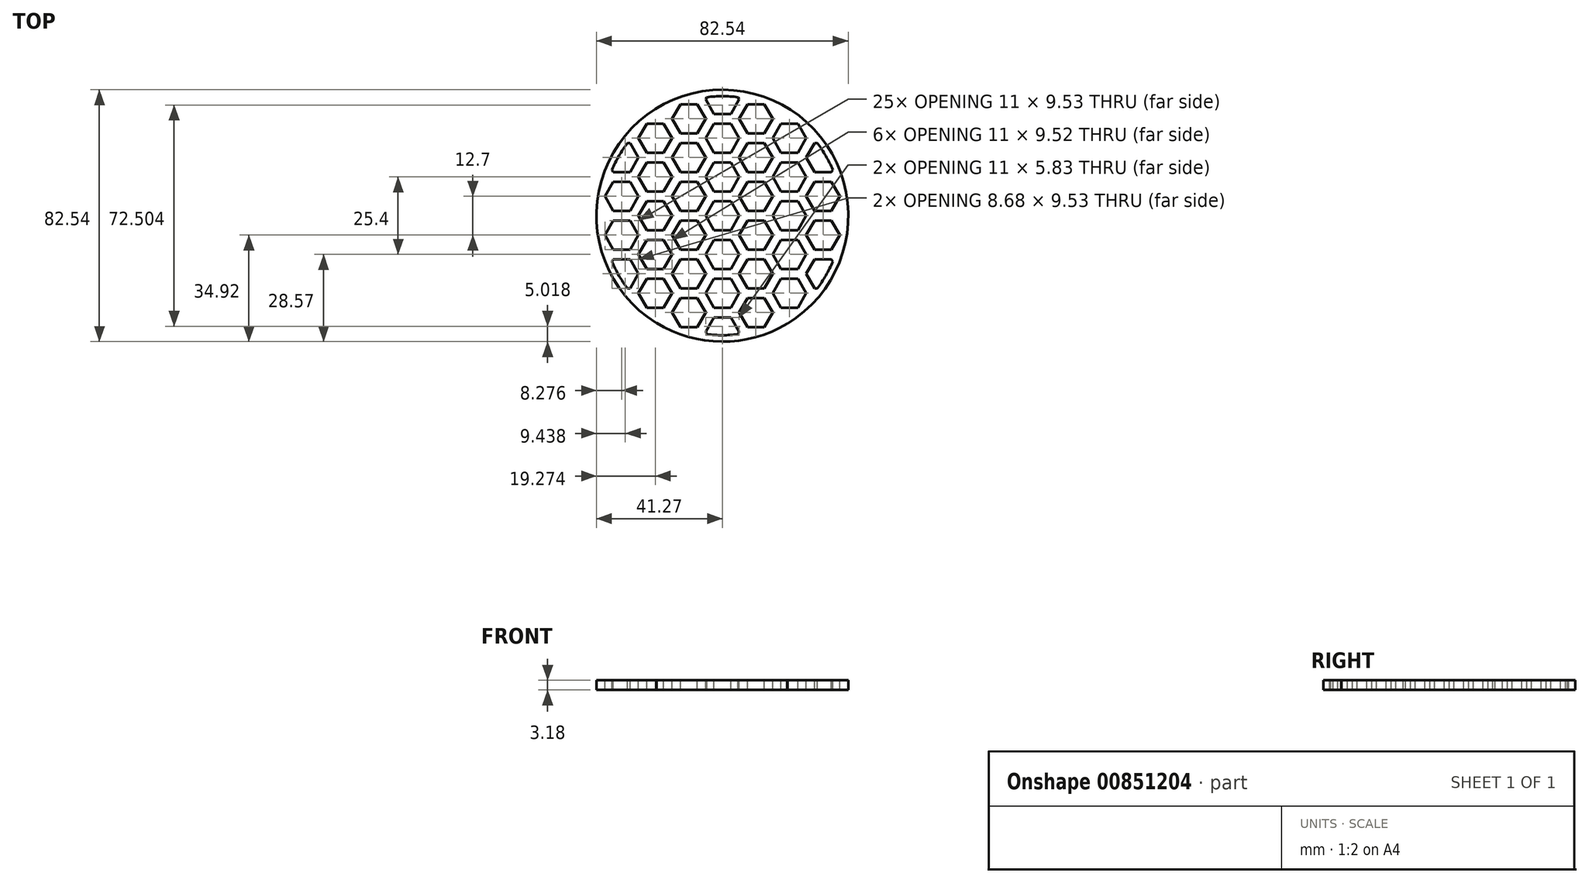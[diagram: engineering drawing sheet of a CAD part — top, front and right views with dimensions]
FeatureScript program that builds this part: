
annotation { "Feature Type Name" : "Feature", "Feature Type Description" : "" }
export const myFeature = defineFeature(function(context is Context, id is Id, definition is map)
    precondition{}
    {
        {
            var Q0;
            Q0=qCreatedBy(makeId("Top.planeOp"),FACE);
            var sketch = newSketch(context, id + "F0", { "sketchPlane" : qUnion([Q0])});
            skCircle(sketch, "E0", {"center": v(0, 0) * mm, "radius": 41.27 * mm});
            skSolve(sketch);
        }
        {
            var Q0;
            Q0 = qSketchRegion(id + "F0", true);
            extrude(context, id + "F1", {"entities" : qUnion([Q0]), "depth" : 3.17 * mm, "offsetDistance" : 25.4 * mm});
        }
        {
            var Q0;
            Q0=makeQuery(id+"F1.opExtrude","CAP_FACE",FACE,{"disambiguationData":[OSD([sQuery(id+"F0.wireOp",EDGE,"E0")])],"isStart":false});
            var sketch = newSketch(context, id + "F2", { "sketchPlane" : qUnion([Q0])});
            skCircle(sketch, "E1.cCircle", {"center": v(-44, -50.8) * mm, "radius": 4.76 * mm, "construction": true});
            skLineSegment(sketch, "E1.0", {"start": v(-46.74, -46.04) * mm, "end": v(-41.24, -46.04) * mm});
            skLineSegment(sketch, "E1.1", {"start": v(-41.24, -46.04) * mm, "end": v(-38.5, -50.8) * mm});
            skLineSegment(sketch, "E1.2", {"start": v(-38.5, -50.8) * mm, "end": v(-41.24, -55.56) * mm});
            skLineSegment(sketch, "E1.3", {"start": v(-41.24, -55.56) * mm, "end": v(-46.74, -55.56) * mm});
            skLineSegment(sketch, "E1.4", {"start": v(-46.74, -55.56) * mm, "end": v(-49.5, -50.8) * mm});
            skLineSegment(sketch, "E1.5", {"start": v(-49.5, -50.8) * mm, "end": v(-46.74, -46.04) * mm});
            skPoint(sketch, "E1.0.midPoint", {"position": v(-44, -46.04) * mm});
            skCircle(sketch, "E2.cCircle", {"center": v(-33, -44.45) * mm, "radius": 4.76 * mm, "construction": true});
            skLineSegment(sketch, "E2.0", {"start": v(-35.74, -39.69) * mm, "end": v(-30.24, -39.69) * mm});
            skLineSegment(sketch, "E2.1", {"start": v(-30.24, -39.69) * mm, "end": v(-27.5, -44.45) * mm});
            skLineSegment(sketch, "E2.2", {"start": v(-27.5, -44.45) * mm, "end": v(-30.24, -49.21) * mm});
            skLineSegment(sketch, "E2.3", {"start": v(-30.24, -49.21) * mm, "end": v(-35.74, -49.21) * mm});
            skLineSegment(sketch, "E2.4", {"start": v(-35.74, -49.21) * mm, "end": v(-38.5, -44.45) * mm});
            skLineSegment(sketch, "E2.5", {"start": v(-38.5, -44.45) * mm, "end": v(-35.74, -39.69) * mm});
            skPoint(sketch, "E2.0.midPoint", {"position": v(-33, -39.69) * mm});
            skLineSegment(sketch, "E3.0.1.0", {"start": v(-46.74, -33.34) * mm, "end": v(-41.24, -33.34) * mm});
            skLineSegment(sketch, "E3.0.1.1", {"start": v(-41.24, -33.34) * mm, "end": v(-38.5, -38.1) * mm});
            skLineSegment(sketch, "E3.0.1.2", {"start": v(-38.5, -38.1) * mm, "end": v(-41.24, -42.86) * mm});
            skCircle(sketch, "E3.0.1.3", {"center": v(-44, -38.1) * mm, "radius": 4.76 * mm, "construction": true});
            skLineSegment(sketch, "E3.0.1.4", {"start": v(-41.24, -42.86) * mm, "end": v(-46.74, -42.86) * mm});
            skLineSegment(sketch, "E3.0.1.5", {"start": v(-46.74, -42.86) * mm, "end": v(-49.5, -38.1) * mm});
            skLineSegment(sketch, "E3.0.1.6", {"start": v(-49.5, -38.1) * mm, "end": v(-46.74, -33.34) * mm});
            skLineSegment(sketch, "E3.0.2.0", {"start": v(-46.74, -20.64) * mm, "end": v(-41.24, -20.64) * mm});
            skLineSegment(sketch, "E3.0.2.1", {"start": v(-41.24, -20.64) * mm, "end": v(-38.5, -25.4) * mm});
            skLineSegment(sketch, "E3.0.2.2", {"start": v(-38.5, -25.4) * mm, "end": v(-41.24, -30.16) * mm});
            skCircle(sketch, "E3.0.2.3", {"center": v(-44, -25.4) * mm, "radius": 4.76 * mm, "construction": true});
            skLineSegment(sketch, "E3.0.2.4", {"start": v(-41.24, -30.16) * mm, "end": v(-46.74, -30.16) * mm});
            skLineSegment(sketch, "E3.0.2.5", {"start": v(-46.74, -30.16) * mm, "end": v(-49.5, -25.4) * mm});
            skLineSegment(sketch, "E3.0.2.6", {"start": v(-49.5, -25.4) * mm, "end": v(-46.74, -20.64) * mm});
            skLineSegment(sketch, "E3.1.0.0", {"start": v(-24.75, -46.04) * mm, "end": v(-19.25, -46.04) * mm});
            skLineSegment(sketch, "E3.1.0.1", {"start": v(-19.25, -46.04) * mm, "end": v(-16.5, -50.8) * mm});
            skLineSegment(sketch, "E3.1.0.2", {"start": v(-16.5, -50.8) * mm, "end": v(-19.25, -55.56) * mm});
            skCircle(sketch, "E3.1.0.3", {"center": v(-22, -50.8) * mm, "radius": 4.76 * mm, "construction": true});
            skLineSegment(sketch, "E3.1.0.4", {"start": v(-19.25, -55.56) * mm, "end": v(-24.75, -55.56) * mm});
            skLineSegment(sketch, "E3.1.0.5", {"start": v(-24.75, -55.56) * mm, "end": v(-27.5, -50.8) * mm});
            skLineSegment(sketch, "E3.1.0.6", {"start": v(-27.5, -50.8) * mm, "end": v(-24.75, -46.04) * mm});
            skLineSegment(sketch, "E3.1.1.0", {"start": v(-24.75, -33.34) * mm, "end": v(-19.25, -33.34) * mm});
            skLineSegment(sketch, "E3.1.1.1", {"start": v(-19.25, -33.34) * mm, "end": v(-16.5, -38.1) * mm});
            skLineSegment(sketch, "E3.1.1.2", {"start": v(-16.5, -38.1) * mm, "end": v(-19.25, -42.86) * mm});
            skCircle(sketch, "E3.1.1.3", {"center": v(-22, -38.1) * mm, "radius": 4.76 * mm, "construction": true});
            skLineSegment(sketch, "E3.1.1.4", {"start": v(-19.25, -42.86) * mm, "end": v(-24.75, -42.86) * mm});
            skLineSegment(sketch, "E3.1.1.5", {"start": v(-24.75, -42.86) * mm, "end": v(-27.5, -38.1) * mm});
            skLineSegment(sketch, "E3.1.1.6", {"start": v(-27.5, -38.1) * mm, "end": v(-24.75, -33.34) * mm});
            skLineSegment(sketch, "E3.1.2.0", {"start": v(-24.75, -20.64) * mm, "end": v(-19.25, -20.64) * mm});
            skLineSegment(sketch, "E3.1.2.1", {"start": v(-19.25, -20.64) * mm, "end": v(-16.5, -25.4) * mm});
            skLineSegment(sketch, "E3.1.2.2", {"start": v(-16.5, -25.4) * mm, "end": v(-19.25, -30.16) * mm});
            skCircle(sketch, "E3.1.2.3", {"center": v(-22, -25.4) * mm, "radius": 4.76 * mm, "construction": true});
            skLineSegment(sketch, "E3.1.2.4", {"start": v(-19.25, -30.16) * mm, "end": v(-24.75, -30.16) * mm});
            skLineSegment(sketch, "E3.1.2.5", {"start": v(-24.75, -30.16) * mm, "end": v(-27.5, -25.4) * mm});
            skLineSegment(sketch, "E3.1.2.6", {"start": v(-27.5, -25.4) * mm, "end": v(-24.75, -20.64) * mm});
            skLineSegment(sketch, "E3.2.0.0", {"start": v(-2.75, -46.04) * mm, "end": v(2.75, -46.04) * mm});
            skLineSegment(sketch, "E3.2.0.1", {"start": v(2.75, -46.04) * mm, "end": v(5.5, -50.8) * mm});
            skLineSegment(sketch, "E3.2.0.2", {"start": v(5.5, -50.8) * mm, "end": v(2.75, -55.56) * mm});
            skCircle(sketch, "E3.2.0.3", {"center": v(0, -50.8) * mm, "radius": 4.76 * mm, "construction": true});
            skLineSegment(sketch, "E3.2.0.4", {"start": v(2.75, -55.56) * mm, "end": v(-2.75, -55.56) * mm});
            skLineSegment(sketch, "E3.2.0.5", {"start": v(-2.75, -55.56) * mm, "end": v(-5.5, -50.8) * mm});
            skLineSegment(sketch, "E3.2.0.6", {"start": v(-5.5, -50.8) * mm, "end": v(-2.75, -46.04) * mm});
            skLineSegment(sketch, "E3.2.1.0", {"start": v(-2.75, -33.34) * mm, "end": v(2.75, -33.34) * mm});
            skLineSegment(sketch, "E3.2.1.1", {"start": v(2.75, -33.34) * mm, "end": v(5.5, -38.1) * mm});
            skLineSegment(sketch, "E3.2.1.2", {"start": v(5.5, -38.1) * mm, "end": v(2.75, -42.86) * mm});
            skCircle(sketch, "E3.2.1.3", {"center": v(0, -38.1) * mm, "radius": 4.76 * mm, "construction": true});
            skLineSegment(sketch, "E3.2.1.4", {"start": v(2.75, -42.86) * mm, "end": v(-2.75, -42.86) * mm});
            skLineSegment(sketch, "E3.2.1.5", {"start": v(-2.75, -42.86) * mm, "end": v(-5.5, -38.1) * mm});
            skLineSegment(sketch, "E3.2.1.6", {"start": v(-5.5, -38.1) * mm, "end": v(-2.75, -33.34) * mm});
            skLineSegment(sketch, "E3.2.2.0", {"start": v(-2.75, -20.64) * mm, "end": v(2.75, -20.64) * mm});
            skLineSegment(sketch, "E3.2.2.1", {"start": v(2.75, -20.64) * mm, "end": v(5.5, -25.4) * mm});
            skLineSegment(sketch, "E3.2.2.2", {"start": v(5.5, -25.4) * mm, "end": v(2.75, -30.16) * mm});
            skCircle(sketch, "E3.2.2.3", {"center": v(0, -25.4) * mm, "radius": 4.76 * mm, "construction": true});
            skLineSegment(sketch, "E3.2.2.4", {"start": v(2.75, -30.16) * mm, "end": v(-2.75, -30.16) * mm});
            skLineSegment(sketch, "E3.2.2.5", {"start": v(-2.75, -30.16) * mm, "end": v(-5.5, -25.4) * mm});
            skLineSegment(sketch, "E3.2.2.6", {"start": v(-5.5, -25.4) * mm, "end": v(-2.75, -20.64) * mm});
            skLineSegment(sketch, "E3.direction1", {"start": v(-46.74, -55.56) * mm, "end": v(-24.75, -55.56) * mm, "construction": true});
            skLineSegment(sketch, "E3.direction2", {"start": v(-46.74, -55.56) * mm, "end": v(-46.74, -42.86) * mm, "construction": true});
            skLineSegment(sketch, "E4.0.0.3", {"start": v(-46.74, -7.94) * mm, "end": v(-41.24, -7.94) * mm});
            skLineSegment(sketch, "E4.3.0.3", {"start": v(-41.24, -7.94) * mm, "end": v(-38.5, -12.7) * mm});
            skLineSegment(sketch, "E4.6.0.3", {"start": v(-38.5, -12.7) * mm, "end": v(-41.24, -17.46) * mm});
            skCircle(sketch, "E4.9.0.3", {"center": v(-44, -12.7) * mm, "radius": 4.76 * mm, "construction": true});
            skLineSegment(sketch, "E4.11.0.3", {"start": v(-41.24, -17.46) * mm, "end": v(-46.74, -17.46) * mm});
            skLineSegment(sketch, "E4.14.0.3", {"start": v(-46.74, -17.46) * mm, "end": v(-49.5, -12.7) * mm});
            skLineSegment(sketch, "E4.17.0.3", {"start": v(-49.5, -12.7) * mm, "end": v(-46.74, -7.94) * mm});
            skLineSegment(sketch, "E4.0.1.3", {"start": v(-24.75, -7.94) * mm, "end": v(-19.25, -7.94) * mm});
            skLineSegment(sketch, "E4.3.1.3", {"start": v(-19.25, -7.94) * mm, "end": v(-16.5, -12.7) * mm});
            skLineSegment(sketch, "E4.6.1.3", {"start": v(-16.5, -12.7) * mm, "end": v(-19.25, -17.46) * mm});
            skCircle(sketch, "E4.9.1.3", {"center": v(-22, -12.7) * mm, "radius": 4.76 * mm, "construction": true});
            skLineSegment(sketch, "E4.11.1.3", {"start": v(-19.25, -17.46) * mm, "end": v(-24.75, -17.46) * mm});
            skLineSegment(sketch, "E4.14.1.3", {"start": v(-24.75, -17.46) * mm, "end": v(-27.5, -12.7) * mm});
            skLineSegment(sketch, "E4.17.1.3", {"start": v(-27.5, -12.7) * mm, "end": v(-24.75, -7.94) * mm});
            skLineSegment(sketch, "E4.0.2.3", {"start": v(-2.75, -7.94) * mm, "end": v(2.75, -7.94) * mm});
            skLineSegment(sketch, "E4.3.2.3", {"start": v(2.75, -7.94) * mm, "end": v(5.5, -12.7) * mm});
            skLineSegment(sketch, "E4.6.2.3", {"start": v(5.5, -12.7) * mm, "end": v(2.75, -17.46) * mm});
            skCircle(sketch, "E4.9.2.3", {"center": v(0, -12.7) * mm, "radius": 4.76 * mm, "construction": true});
            skLineSegment(sketch, "E4.11.2.3", {"start": v(2.75, -17.46) * mm, "end": v(-2.75, -17.46) * mm});
            skLineSegment(sketch, "E4.14.2.3", {"start": v(-2.75, -17.46) * mm, "end": v(-5.5, -12.7) * mm});
            skLineSegment(sketch, "E4.17.2.3", {"start": v(-5.5, -12.7) * mm, "end": v(-2.75, -7.94) * mm});
            skCircle(sketch, "E5.0.1.0", {"center": v(-33, -31.75) * mm, "radius": 4.76 * mm, "construction": true});
            skLineSegment(sketch, "E5.0.1.1", {"start": v(-38.5, -31.75) * mm, "end": v(-35.74, -26.99) * mm});
            skLineSegment(sketch, "E5.0.1.2", {"start": v(-35.74, -26.99) * mm, "end": v(-30.24, -26.99) * mm});
            skLineSegment(sketch, "E5.0.1.3", {"start": v(-30.24, -26.99) * mm, "end": v(-27.5, -31.75) * mm});
            skLineSegment(sketch, "E5.0.1.4", {"start": v(-27.5, -31.75) * mm, "end": v(-30.24, -36.51) * mm});
            skLineSegment(sketch, "E5.0.1.5", {"start": v(-30.24, -36.51) * mm, "end": v(-35.74, -36.51) * mm});
            skLineSegment(sketch, "E5.0.1.6", {"start": v(-35.74, -36.51) * mm, "end": v(-38.5, -31.75) * mm});
            skCircle(sketch, "E5.0.2.0", {"center": v(-33, -19.05) * mm, "radius": 4.76 * mm, "construction": true});
            skLineSegment(sketch, "E5.0.2.1", {"start": v(-38.5, -19.05) * mm, "end": v(-35.74, -14.29) * mm});
            skLineSegment(sketch, "E5.0.2.2", {"start": v(-35.74, -14.29) * mm, "end": v(-30.24, -14.29) * mm});
            skLineSegment(sketch, "E5.0.2.3", {"start": v(-30.24, -14.29) * mm, "end": v(-27.5, -19.05) * mm});
            skLineSegment(sketch, "E5.0.2.4", {"start": v(-27.5, -19.05) * mm, "end": v(-30.24, -23.81) * mm});
            skLineSegment(sketch, "E5.0.2.5", {"start": v(-30.24, -23.81) * mm, "end": v(-35.74, -23.81) * mm});
            skLineSegment(sketch, "E5.0.2.6", {"start": v(-35.74, -23.81) * mm, "end": v(-38.5, -19.05) * mm});
            skCircle(sketch, "E5.0.3.0", {"center": v(-33, -6.35) * mm, "radius": 4.76 * mm, "construction": true});
            skLineSegment(sketch, "E5.0.3.1", {"start": v(-38.5, -6.35) * mm, "end": v(-35.74, -1.59) * mm});
            skLineSegment(sketch, "E5.0.3.2", {"start": v(-35.74, -1.59) * mm, "end": v(-30.24, -1.59) * mm});
            skLineSegment(sketch, "E5.0.3.3", {"start": v(-30.24, -1.59) * mm, "end": v(-27.5, -6.35) * mm});
            skLineSegment(sketch, "E5.0.3.4", {"start": v(-27.5, -6.35) * mm, "end": v(-30.24, -11.11) * mm});
            skLineSegment(sketch, "E5.0.3.5", {"start": v(-30.24, -11.11) * mm, "end": v(-35.74, -11.11) * mm});
            skLineSegment(sketch, "E5.0.3.6", {"start": v(-35.74, -11.11) * mm, "end": v(-38.5, -6.35) * mm});
            skCircle(sketch, "E5.1.0.0", {"center": v(-11, -44.45) * mm, "radius": 4.76 * mm, "construction": true});
            skLineSegment(sketch, "E5.1.0.1", {"start": v(-16.5, -44.45) * mm, "end": v(-13.75, -39.69) * mm});
            skLineSegment(sketch, "E5.1.0.2", {"start": v(-13.75, -39.69) * mm, "end": v(-8.25, -39.69) * mm});
            skLineSegment(sketch, "E5.1.0.3", {"start": v(-8.25, -39.69) * mm, "end": v(-5.5, -44.45) * mm});
            skLineSegment(sketch, "E5.1.0.4", {"start": v(-5.5, -44.45) * mm, "end": v(-8.25, -49.21) * mm});
            skLineSegment(sketch, "E5.1.0.5", {"start": v(-8.25, -49.21) * mm, "end": v(-13.75, -49.21) * mm});
            skLineSegment(sketch, "E5.1.0.6", {"start": v(-13.75, -49.21) * mm, "end": v(-16.5, -44.45) * mm});
            skCircle(sketch, "E5.1.1.0", {"center": v(-11, -31.75) * mm, "radius": 4.76 * mm, "construction": true});
            skLineSegment(sketch, "E5.1.1.1", {"start": v(-16.5, -31.75) * mm, "end": v(-13.75, -26.99) * mm});
            skLineSegment(sketch, "E5.1.1.2", {"start": v(-13.75, -26.99) * mm, "end": v(-8.25, -26.99) * mm});
            skLineSegment(sketch, "E5.1.1.3", {"start": v(-8.25, -26.99) * mm, "end": v(-5.5, -31.75) * mm});
            skLineSegment(sketch, "E5.1.1.4", {"start": v(-5.5, -31.75) * mm, "end": v(-8.25, -36.51) * mm});
            skLineSegment(sketch, "E5.1.1.5", {"start": v(-8.25, -36.51) * mm, "end": v(-13.75, -36.51) * mm});
            skLineSegment(sketch, "E5.1.1.6", {"start": v(-13.75, -36.51) * mm, "end": v(-16.5, -31.75) * mm});
            skCircle(sketch, "E5.1.2.0", {"center": v(-11, -19.05) * mm, "radius": 4.76 * mm, "construction": true});
            skLineSegment(sketch, "E5.1.2.1", {"start": v(-16.5, -19.05) * mm, "end": v(-13.75, -14.29) * mm});
            skLineSegment(sketch, "E5.1.2.2", {"start": v(-13.75, -14.29) * mm, "end": v(-8.25, -14.29) * mm});
            skLineSegment(sketch, "E5.1.2.3", {"start": v(-8.25, -14.29) * mm, "end": v(-5.5, -19.05) * mm});
            skLineSegment(sketch, "E5.1.2.4", {"start": v(-5.5, -19.05) * mm, "end": v(-8.25, -23.81) * mm});
            skLineSegment(sketch, "E5.1.2.5", {"start": v(-8.25, -23.81) * mm, "end": v(-13.75, -23.81) * mm});
            skLineSegment(sketch, "E5.1.2.6", {"start": v(-13.75, -23.81) * mm, "end": v(-16.5, -19.05) * mm});
            skCircle(sketch, "E5.1.3.0", {"center": v(-11, -6.35) * mm, "radius": 4.76 * mm, "construction": true});
            skLineSegment(sketch, "E5.1.3.1", {"start": v(-16.5, -6.35) * mm, "end": v(-13.75, -1.59) * mm});
            skLineSegment(sketch, "E5.1.3.2", {"start": v(-13.75, -1.59) * mm, "end": v(-8.25, -1.59) * mm});
            skLineSegment(sketch, "E5.1.3.3", {"start": v(-8.25, -1.59) * mm, "end": v(-5.5, -6.35) * mm});
            skLineSegment(sketch, "E5.1.3.4", {"start": v(-5.5, -6.35) * mm, "end": v(-8.25, -11.11) * mm});
            skLineSegment(sketch, "E5.1.3.5", {"start": v(-8.25, -11.11) * mm, "end": v(-13.75, -11.11) * mm});
            skLineSegment(sketch, "E5.1.3.6", {"start": v(-13.75, -11.11) * mm, "end": v(-16.5, -6.35) * mm});
            skLineSegment(sketch, "E5.direction1", {"start": v(-35.74, -49.21) * mm, "end": v(-13.75, -49.21) * mm, "construction": true});
            skLineSegment(sketch, "E5.direction2", {"start": v(-35.74, -49.21) * mm, "end": v(-35.74, -36.51) * mm, "construction": true});
            skLineSegment(sketch, "E6.0.3.0", {"start": v(19.25, -46.04) * mm, "end": v(24.75, -46.04) * mm});
            skLineSegment(sketch, "E6.3.3.0", {"start": v(24.75, -46.04) * mm, "end": v(27.5, -50.8) * mm});
            skLineSegment(sketch, "E6.6.3.0", {"start": v(27.5, -50.8) * mm, "end": v(24.75, -55.56) * mm});
            skCircle(sketch, "E6.9.3.0", {"center": v(22, -50.8) * mm, "radius": 4.76 * mm, "construction": true});
            skLineSegment(sketch, "E6.11.3.0", {"start": v(24.75, -55.56) * mm, "end": v(19.25, -55.56) * mm});
            skLineSegment(sketch, "E6.14.3.0", {"start": v(19.25, -55.56) * mm, "end": v(16.5, -50.8) * mm});
            skLineSegment(sketch, "E6.17.3.0", {"start": v(16.5, -50.8) * mm, "end": v(19.25, -46.04) * mm});
            skLineSegment(sketch, "E6.0.3.1", {"start": v(19.25, -33.34) * mm, "end": v(24.75, -33.34) * mm});
            skLineSegment(sketch, "E6.3.3.1", {"start": v(24.75, -33.34) * mm, "end": v(27.5, -38.1) * mm});
            skLineSegment(sketch, "E6.6.3.1", {"start": v(27.5, -38.1) * mm, "end": v(24.75, -42.86) * mm});
            skCircle(sketch, "E6.9.3.1", {"center": v(22, -38.1) * mm, "radius": 4.76 * mm, "construction": true});
            skLineSegment(sketch, "E6.11.3.1", {"start": v(24.75, -42.86) * mm, "end": v(19.25, -42.86) * mm});
            skLineSegment(sketch, "E6.14.3.1", {"start": v(19.25, -42.86) * mm, "end": v(16.5, -38.1) * mm});
            skLineSegment(sketch, "E6.17.3.1", {"start": v(16.5, -38.1) * mm, "end": v(19.25, -33.34) * mm});
            skLineSegment(sketch, "E6.0.3.2", {"start": v(19.25, -20.64) * mm, "end": v(24.75, -20.64) * mm});
            skLineSegment(sketch, "E6.3.3.2", {"start": v(24.75, -20.64) * mm, "end": v(27.5, -25.4) * mm});
            skLineSegment(sketch, "E6.6.3.2", {"start": v(27.5, -25.4) * mm, "end": v(24.75, -30.16) * mm});
            skCircle(sketch, "E6.9.3.2", {"center": v(22, -25.4) * mm, "radius": 4.76 * mm, "construction": true});
            skLineSegment(sketch, "E6.11.3.2", {"start": v(24.75, -30.16) * mm, "end": v(19.25, -30.16) * mm});
            skLineSegment(sketch, "E6.14.3.2", {"start": v(19.25, -30.16) * mm, "end": v(16.5, -25.4) * mm});
            skLineSegment(sketch, "E6.17.3.2", {"start": v(16.5, -25.4) * mm, "end": v(19.25, -20.64) * mm});
            skLineSegment(sketch, "E6.0.3.3", {"start": v(19.25, -7.94) * mm, "end": v(24.75, -7.94) * mm});
            skLineSegment(sketch, "E6.3.3.3", {"start": v(24.75, -7.94) * mm, "end": v(27.5, -12.7) * mm});
            skLineSegment(sketch, "E6.6.3.3", {"start": v(27.5, -12.7) * mm, "end": v(24.75, -17.46) * mm});
            skCircle(sketch, "E6.9.3.3", {"center": v(22, -12.7) * mm, "radius": 4.76 * mm, "construction": true});
            skLineSegment(sketch, "E6.11.3.3", {"start": v(24.75, -17.46) * mm, "end": v(19.25, -17.46) * mm});
            skLineSegment(sketch, "E6.14.3.3", {"start": v(19.25, -17.46) * mm, "end": v(16.5, -12.7) * mm});
            skLineSegment(sketch, "E6.17.3.3", {"start": v(16.5, -12.7) * mm, "end": v(19.25, -7.94) * mm});
            skLineSegment(sketch, "E6.0.4.0", {"start": v(41.24, -46.04) * mm, "end": v(46.74, -46.04) * mm});
            skLineSegment(sketch, "E6.3.4.0", {"start": v(46.74, -46.04) * mm, "end": v(49.5, -50.8) * mm});
            skLineSegment(sketch, "E6.6.4.0", {"start": v(49.5, -50.8) * mm, "end": v(46.74, -55.56) * mm});
            skCircle(sketch, "E6.9.4.0", {"center": v(44, -50.8) * mm, "radius": 4.76 * mm, "construction": true});
            skLineSegment(sketch, "E6.11.4.0", {"start": v(46.74, -55.56) * mm, "end": v(41.24, -55.56) * mm});
            skLineSegment(sketch, "E6.14.4.0", {"start": v(41.24, -55.56) * mm, "end": v(38.5, -50.8) * mm});
            skLineSegment(sketch, "E6.17.4.0", {"start": v(38.5, -50.8) * mm, "end": v(41.24, -46.04) * mm});
            skLineSegment(sketch, "E6.0.4.1", {"start": v(41.24, -33.34) * mm, "end": v(46.74, -33.34) * mm});
            skLineSegment(sketch, "E6.3.4.1", {"start": v(46.74, -33.34) * mm, "end": v(49.5, -38.1) * mm});
            skLineSegment(sketch, "E6.6.4.1", {"start": v(49.5, -38.1) * mm, "end": v(46.74, -42.86) * mm});
            skCircle(sketch, "E6.9.4.1", {"center": v(44, -38.1) * mm, "radius": 4.76 * mm, "construction": true});
            skLineSegment(sketch, "E6.11.4.1", {"start": v(46.74, -42.86) * mm, "end": v(41.24, -42.86) * mm});
            skLineSegment(sketch, "E6.14.4.1", {"start": v(41.24, -42.86) * mm, "end": v(38.5, -38.1) * mm});
            skLineSegment(sketch, "E6.17.4.1", {"start": v(38.5, -38.1) * mm, "end": v(41.24, -33.34) * mm});
            skLineSegment(sketch, "E6.0.4.2", {"start": v(41.24, -20.64) * mm, "end": v(46.74, -20.64) * mm});
            skLineSegment(sketch, "E6.3.4.2", {"start": v(46.74, -20.64) * mm, "end": v(49.5, -25.4) * mm});
            skLineSegment(sketch, "E6.6.4.2", {"start": v(49.5, -25.4) * mm, "end": v(46.74, -30.16) * mm});
            skCircle(sketch, "E6.9.4.2", {"center": v(44, -25.4) * mm, "radius": 4.76 * mm, "construction": true});
            skLineSegment(sketch, "E6.11.4.2", {"start": v(46.74, -30.16) * mm, "end": v(41.24, -30.16) * mm});
            skLineSegment(sketch, "E6.14.4.2", {"start": v(41.24, -30.16) * mm, "end": v(38.5, -25.4) * mm});
            skLineSegment(sketch, "E6.17.4.2", {"start": v(38.5, -25.4) * mm, "end": v(41.24, -20.64) * mm});
            skLineSegment(sketch, "E6.0.4.3", {"start": v(41.24, -7.94) * mm, "end": v(46.74, -7.94) * mm});
            skLineSegment(sketch, "E6.3.4.3", {"start": v(46.74, -7.94) * mm, "end": v(49.5, -12.7) * mm});
            skLineSegment(sketch, "E6.6.4.3", {"start": v(49.5, -12.7) * mm, "end": v(46.74, -17.46) * mm});
            skCircle(sketch, "E6.9.4.3", {"center": v(44, -12.7) * mm, "radius": 4.76 * mm, "construction": true});
            skLineSegment(sketch, "E6.11.4.3", {"start": v(46.74, -17.46) * mm, "end": v(41.24, -17.46) * mm});
            skLineSegment(sketch, "E6.14.4.3", {"start": v(41.24, -17.46) * mm, "end": v(38.5, -12.7) * mm});
            skLineSegment(sketch, "E6.17.4.3", {"start": v(38.5, -12.7) * mm, "end": v(41.24, -7.94) * mm});
            skLineSegment(sketch, "E6.0.5.0", {"start": v(63.24, -46.04) * mm, "end": v(68.74, -46.04) * mm});
            skLineSegment(sketch, "E6.3.5.0", {"start": v(68.74, -46.04) * mm, "end": v(71.49, -50.8) * mm});
            skLineSegment(sketch, "E6.6.5.0", {"start": v(71.49, -50.8) * mm, "end": v(68.74, -55.56) * mm});
            skCircle(sketch, "E6.9.5.0", {"center": v(65.99, -50.8) * mm, "radius": 4.76 * mm, "construction": true});
            skLineSegment(sketch, "E6.11.5.0", {"start": v(68.74, -55.56) * mm, "end": v(63.24, -55.56) * mm});
            skLineSegment(sketch, "E6.14.5.0", {"start": v(63.24, -55.56) * mm, "end": v(60.49, -50.8) * mm});
            skLineSegment(sketch, "E6.17.5.0", {"start": v(60.49, -50.8) * mm, "end": v(63.24, -46.04) * mm});
            skLineSegment(sketch, "E6.0.5.1", {"start": v(63.24, -33.34) * mm, "end": v(68.74, -33.34) * mm});
            skLineSegment(sketch, "E6.3.5.1", {"start": v(68.74, -33.34) * mm, "end": v(71.49, -38.1) * mm});
            skLineSegment(sketch, "E6.6.5.1", {"start": v(71.49, -38.1) * mm, "end": v(68.74, -42.86) * mm});
            skCircle(sketch, "E6.9.5.1", {"center": v(65.99, -38.1) * mm, "radius": 4.76 * mm, "construction": true});
            skLineSegment(sketch, "E6.11.5.1", {"start": v(68.74, -42.86) * mm, "end": v(63.24, -42.86) * mm});
            skLineSegment(sketch, "E6.14.5.1", {"start": v(63.24, -42.86) * mm, "end": v(60.49, -38.1) * mm});
            skLineSegment(sketch, "E6.17.5.1", {"start": v(60.49, -38.1) * mm, "end": v(63.24, -33.34) * mm});
            skLineSegment(sketch, "E6.0.5.2", {"start": v(63.24, -20.64) * mm, "end": v(68.74, -20.64) * mm});
            skLineSegment(sketch, "E6.3.5.2", {"start": v(68.74, -20.64) * mm, "end": v(71.49, -25.4) * mm});
            skLineSegment(sketch, "E6.6.5.2", {"start": v(71.49, -25.4) * mm, "end": v(68.74, -30.16) * mm});
            skCircle(sketch, "E6.9.5.2", {"center": v(65.99, -25.4) * mm, "radius": 4.76 * mm, "construction": true});
            skLineSegment(sketch, "E6.11.5.2", {"start": v(68.74, -30.16) * mm, "end": v(63.24, -30.16) * mm});
            skLineSegment(sketch, "E6.14.5.2", {"start": v(63.24, -30.16) * mm, "end": v(60.49, -25.4) * mm});
            skLineSegment(sketch, "E6.17.5.2", {"start": v(60.49, -25.4) * mm, "end": v(63.24, -20.64) * mm});
            skLineSegment(sketch, "E6.0.5.3", {"start": v(63.24, -7.94) * mm, "end": v(68.74, -7.94) * mm});
            skLineSegment(sketch, "E6.3.5.3", {"start": v(68.74, -7.94) * mm, "end": v(71.49, -12.7) * mm});
            skLineSegment(sketch, "E6.6.5.3", {"start": v(71.49, -12.7) * mm, "end": v(68.74, -17.46) * mm});
            skCircle(sketch, "E6.9.5.3", {"center": v(65.99, -12.7) * mm, "radius": 4.76 * mm, "construction": true});
            skLineSegment(sketch, "E6.11.5.3", {"start": v(68.74, -17.46) * mm, "end": v(63.24, -17.46) * mm});
            skLineSegment(sketch, "E6.14.5.3", {"start": v(63.24, -17.46) * mm, "end": v(60.49, -12.7) * mm});
            skLineSegment(sketch, "E6.17.5.3", {"start": v(60.49, -12.7) * mm, "end": v(63.24, -7.94) * mm});
            skCircle(sketch, "E7.0.2.0", {"center": v(11, -44.45) * mm, "radius": 4.76 * mm, "construction": true});
            skLineSegment(sketch, "E7.2.2.0", {"start": v(5.5, -44.45) * mm, "end": v(8.25, -39.69) * mm});
            skLineSegment(sketch, "E7.5.2.0", {"start": v(8.25, -39.69) * mm, "end": v(13.75, -39.69) * mm});
            skLineSegment(sketch, "E7.8.2.0", {"start": v(13.75, -39.69) * mm, "end": v(16.5, -44.45) * mm});
            skLineSegment(sketch, "E7.11.2.0", {"start": v(16.5, -44.45) * mm, "end": v(13.75, -49.21) * mm});
            skLineSegment(sketch, "E7.14.2.0", {"start": v(13.75, -49.21) * mm, "end": v(8.25, -49.21) * mm});
            skLineSegment(sketch, "E7.17.2.0", {"start": v(8.25, -49.21) * mm, "end": v(5.5, -44.45) * mm});
            skCircle(sketch, "E7.0.2.1", {"center": v(11, -31.75) * mm, "radius": 4.76 * mm, "construction": true});
            skLineSegment(sketch, "E7.2.2.1", {"start": v(5.5, -31.75) * mm, "end": v(8.25, -26.99) * mm});
            skLineSegment(sketch, "E7.5.2.1", {"start": v(8.25, -26.99) * mm, "end": v(13.75, -26.99) * mm});
            skLineSegment(sketch, "E7.8.2.1", {"start": v(13.75, -26.99) * mm, "end": v(16.5, -31.75) * mm});
            skLineSegment(sketch, "E7.11.2.1", {"start": v(16.5, -31.75) * mm, "end": v(13.75, -36.51) * mm});
            skLineSegment(sketch, "E7.14.2.1", {"start": v(13.75, -36.51) * mm, "end": v(8.25, -36.51) * mm});
            skLineSegment(sketch, "E7.17.2.1", {"start": v(8.25, -36.51) * mm, "end": v(5.5, -31.75) * mm});
            skCircle(sketch, "E7.0.2.2", {"center": v(11, -19.05) * mm, "radius": 4.76 * mm, "construction": true});
            skLineSegment(sketch, "E7.2.2.2", {"start": v(5.5, -19.05) * mm, "end": v(8.25, -14.29) * mm});
            skLineSegment(sketch, "E7.5.2.2", {"start": v(8.25, -14.29) * mm, "end": v(13.75, -14.29) * mm});
            skLineSegment(sketch, "E7.8.2.2", {"start": v(13.75, -14.29) * mm, "end": v(16.5, -19.05) * mm});
            skLineSegment(sketch, "E7.11.2.2", {"start": v(16.5, -19.05) * mm, "end": v(13.75, -23.81) * mm});
            skLineSegment(sketch, "E7.14.2.2", {"start": v(13.75, -23.81) * mm, "end": v(8.25, -23.81) * mm});
            skLineSegment(sketch, "E7.17.2.2", {"start": v(8.25, -23.81) * mm, "end": v(5.5, -19.05) * mm});
            skCircle(sketch, "E7.0.2.3", {"center": v(11, -6.35) * mm, "radius": 4.76 * mm, "construction": true});
            skLineSegment(sketch, "E7.2.2.3", {"start": v(5.5, -6.35) * mm, "end": v(8.25, -1.59) * mm});
            skLineSegment(sketch, "E7.5.2.3", {"start": v(8.25, -1.59) * mm, "end": v(13.75, -1.59) * mm});
            skLineSegment(sketch, "E7.8.2.3", {"start": v(13.75, -1.59) * mm, "end": v(16.5, -6.35) * mm});
            skLineSegment(sketch, "E7.11.2.3", {"start": v(16.5, -6.35) * mm, "end": v(13.75, -11.11) * mm});
            skLineSegment(sketch, "E7.14.2.3", {"start": v(13.75, -11.11) * mm, "end": v(8.25, -11.11) * mm});
            skLineSegment(sketch, "E7.17.2.3", {"start": v(8.25, -11.11) * mm, "end": v(5.5, -6.35) * mm});
            skCircle(sketch, "E7.0.3.0", {"center": v(33, -44.45) * mm, "radius": 4.76 * mm, "construction": true});
            skLineSegment(sketch, "E7.2.3.0", {"start": v(27.5, -44.45) * mm, "end": v(30.25, -39.69) * mm});
            skLineSegment(sketch, "E7.5.3.0", {"start": v(30.25, -39.69) * mm, "end": v(35.74, -39.69) * mm});
            skLineSegment(sketch, "E7.8.3.0", {"start": v(35.74, -39.69) * mm, "end": v(38.5, -44.45) * mm});
            skLineSegment(sketch, "E7.11.3.0", {"start": v(38.5, -44.45) * mm, "end": v(35.74, -49.21) * mm});
            skLineSegment(sketch, "E7.14.3.0", {"start": v(35.74, -49.21) * mm, "end": v(30.25, -49.21) * mm});
            skLineSegment(sketch, "E7.17.3.0", {"start": v(30.25, -49.21) * mm, "end": v(27.5, -44.45) * mm});
            skCircle(sketch, "E7.0.3.1", {"center": v(33, -31.75) * mm, "radius": 4.76 * mm, "construction": true});
            skLineSegment(sketch, "E7.2.3.1", {"start": v(27.5, -31.75) * mm, "end": v(30.25, -26.99) * mm});
            skLineSegment(sketch, "E7.5.3.1", {"start": v(30.25, -26.99) * mm, "end": v(35.74, -26.99) * mm});
            skLineSegment(sketch, "E7.8.3.1", {"start": v(35.74, -26.99) * mm, "end": v(38.5, -31.75) * mm});
            skLineSegment(sketch, "E7.11.3.1", {"start": v(38.5, -31.75) * mm, "end": v(35.74, -36.51) * mm});
            skLineSegment(sketch, "E7.14.3.1", {"start": v(35.74, -36.51) * mm, "end": v(30.25, -36.51) * mm});
            skLineSegment(sketch, "E7.17.3.1", {"start": v(30.25, -36.51) * mm, "end": v(27.5, -31.75) * mm});
            skCircle(sketch, "E7.0.3.2", {"center": v(33, -19.05) * mm, "radius": 4.76 * mm, "construction": true});
            skLineSegment(sketch, "E7.2.3.2", {"start": v(27.5, -19.05) * mm, "end": v(30.25, -14.29) * mm});
            skLineSegment(sketch, "E7.5.3.2", {"start": v(30.25, -14.29) * mm, "end": v(35.74, -14.29) * mm});
            skLineSegment(sketch, "E7.8.3.2", {"start": v(35.74, -14.29) * mm, "end": v(38.5, -19.05) * mm});
            skLineSegment(sketch, "E7.11.3.2", {"start": v(38.5, -19.05) * mm, "end": v(35.74, -23.81) * mm});
            skLineSegment(sketch, "E7.14.3.2", {"start": v(35.74, -23.81) * mm, "end": v(30.25, -23.81) * mm});
            skLineSegment(sketch, "E7.17.3.2", {"start": v(30.25, -23.81) * mm, "end": v(27.5, -19.05) * mm});
            skCircle(sketch, "E7.0.3.3", {"center": v(33, -6.35) * mm, "radius": 4.76 * mm, "construction": true});
            skLineSegment(sketch, "E7.2.3.3", {"start": v(27.5, -6.35) * mm, "end": v(30.25, -1.59) * mm});
            skLineSegment(sketch, "E7.5.3.3", {"start": v(30.25, -1.59) * mm, "end": v(35.74, -1.59) * mm});
            skLineSegment(sketch, "E7.8.3.3", {"start": v(35.74, -1.59) * mm, "end": v(38.5, -6.35) * mm});
            skLineSegment(sketch, "E7.11.3.3", {"start": v(38.5, -6.35) * mm, "end": v(35.74, -11.11) * mm});
            skLineSegment(sketch, "E7.14.3.3", {"start": v(35.74, -11.11) * mm, "end": v(30.25, -11.11) * mm});
            skLineSegment(sketch, "E7.17.3.3", {"start": v(30.25, -11.11) * mm, "end": v(27.5, -6.35) * mm});
            skCircle(sketch, "E7.0.4.0", {"center": v(55, -44.45) * mm, "radius": 4.76 * mm, "construction": true});
            skLineSegment(sketch, "E7.2.4.0", {"start": v(49.5, -44.45) * mm, "end": v(52.24, -39.69) * mm});
            skLineSegment(sketch, "E7.5.4.0", {"start": v(52.24, -39.69) * mm, "end": v(57.74, -39.69) * mm});
            skLineSegment(sketch, "E7.8.4.0", {"start": v(57.74, -39.69) * mm, "end": v(60.5, -44.45) * mm});
            skLineSegment(sketch, "E7.11.4.0", {"start": v(60.5, -44.45) * mm, "end": v(57.74, -49.21) * mm});
            skLineSegment(sketch, "E7.14.4.0", {"start": v(57.74, -49.21) * mm, "end": v(52.24, -49.21) * mm});
            skLineSegment(sketch, "E7.17.4.0", {"start": v(52.24, -49.21) * mm, "end": v(49.5, -44.45) * mm});
            skCircle(sketch, "E7.0.4.1", {"center": v(55, -31.75) * mm, "radius": 4.76 * mm, "construction": true});
            skLineSegment(sketch, "E7.2.4.1", {"start": v(49.5, -31.75) * mm, "end": v(52.24, -26.99) * mm});
            skLineSegment(sketch, "E7.5.4.1", {"start": v(52.24, -26.99) * mm, "end": v(57.74, -26.99) * mm});
            skLineSegment(sketch, "E7.8.4.1", {"start": v(57.74, -26.99) * mm, "end": v(60.5, -31.75) * mm});
            skLineSegment(sketch, "E7.11.4.1", {"start": v(60.5, -31.75) * mm, "end": v(57.74, -36.51) * mm});
            skLineSegment(sketch, "E7.14.4.1", {"start": v(57.74, -36.51) * mm, "end": v(52.24, -36.51) * mm});
            skLineSegment(sketch, "E7.17.4.1", {"start": v(52.24, -36.51) * mm, "end": v(49.5, -31.75) * mm});
            skCircle(sketch, "E7.0.4.2", {"center": v(55, -19.05) * mm, "radius": 4.76 * mm, "construction": true});
            skLineSegment(sketch, "E7.2.4.2", {"start": v(49.5, -19.05) * mm, "end": v(52.24, -14.29) * mm});
            skLineSegment(sketch, "E7.5.4.2", {"start": v(52.24, -14.29) * mm, "end": v(57.74, -14.29) * mm});
            skLineSegment(sketch, "E7.8.4.2", {"start": v(57.74, -14.29) * mm, "end": v(60.5, -19.05) * mm});
            skLineSegment(sketch, "E7.11.4.2", {"start": v(60.5, -19.05) * mm, "end": v(57.74, -23.81) * mm});
            skLineSegment(sketch, "E7.14.4.2", {"start": v(57.74, -23.81) * mm, "end": v(52.24, -23.81) * mm});
            skLineSegment(sketch, "E7.17.4.2", {"start": v(52.24, -23.81) * mm, "end": v(49.5, -19.05) * mm});
            skCircle(sketch, "E7.0.4.3", {"center": v(55, -6.35) * mm, "radius": 4.76 * mm, "construction": true});
            skLineSegment(sketch, "E7.2.4.3", {"start": v(49.5, -6.35) * mm, "end": v(52.24, -1.59) * mm});
            skLineSegment(sketch, "E7.5.4.3", {"start": v(52.24, -1.59) * mm, "end": v(57.74, -1.59) * mm});
            skLineSegment(sketch, "E7.8.4.3", {"start": v(57.74, -1.59) * mm, "end": v(60.5, -6.35) * mm});
            skLineSegment(sketch, "E7.11.4.3", {"start": v(60.5, -6.35) * mm, "end": v(57.74, -11.11) * mm});
            skLineSegment(sketch, "E7.14.4.3", {"start": v(57.74, -11.11) * mm, "end": v(52.24, -11.11) * mm});
            skLineSegment(sketch, "E7.17.4.3", {"start": v(52.24, -11.11) * mm, "end": v(49.5, -6.35) * mm});
            skLineSegment(sketch, "E8.0.0.4", {"start": v(-46.74, 4.76) * mm, "end": v(-41.24, 4.76) * mm});
            skLineSegment(sketch, "E8.3.0.4", {"start": v(-41.24, 4.76) * mm, "end": v(-38.5, 0) * mm});
            skLineSegment(sketch, "E8.6.0.4", {"start": v(-38.5, 0) * mm, "end": v(-41.24, -4.76) * mm});
            skCircle(sketch, "E8.9.0.4", {"center": v(-44, 0) * mm, "radius": 4.76 * mm, "construction": true});
            skLineSegment(sketch, "E8.11.0.4", {"start": v(-41.24, -4.76) * mm, "end": v(-46.74, -4.76) * mm});
            skLineSegment(sketch, "E8.14.0.4", {"start": v(-46.74, -4.76) * mm, "end": v(-49.5, 0) * mm});
            skLineSegment(sketch, "E8.17.0.4", {"start": v(-49.5, 0) * mm, "end": v(-46.74, 4.76) * mm});
            skLineSegment(sketch, "E8.0.0.5", {"start": v(-46.74, 17.46) * mm, "end": v(-41.24, 17.46) * mm});
            skLineSegment(sketch, "E8.3.0.5", {"start": v(-41.24, 17.46) * mm, "end": v(-38.5, 12.7) * mm});
            skLineSegment(sketch, "E8.6.0.5", {"start": v(-38.5, 12.7) * mm, "end": v(-41.24, 7.94) * mm});
            skCircle(sketch, "E8.9.0.5", {"center": v(-44, 12.7) * mm, "radius": 4.76 * mm, "construction": true});
            skLineSegment(sketch, "E8.11.0.5", {"start": v(-41.24, 7.94) * mm, "end": v(-46.74, 7.94) * mm});
            skLineSegment(sketch, "E8.14.0.5", {"start": v(-46.74, 7.94) * mm, "end": v(-49.5, 12.7) * mm});
            skLineSegment(sketch, "E8.17.0.5", {"start": v(-49.5, 12.7) * mm, "end": v(-46.74, 17.46) * mm});
            skLineSegment(sketch, "E8.0.0.6", {"start": v(-46.74, 30.16) * mm, "end": v(-41.24, 30.16) * mm});
            skLineSegment(sketch, "E8.3.0.6", {"start": v(-41.24, 30.16) * mm, "end": v(-38.5, 25.4) * mm});
            skLineSegment(sketch, "E8.6.0.6", {"start": v(-38.5, 25.4) * mm, "end": v(-41.24, 20.64) * mm});
            skCircle(sketch, "E8.9.0.6", {"center": v(-44, 25.4) * mm, "radius": 4.76 * mm, "construction": true});
            skLineSegment(sketch, "E8.11.0.6", {"start": v(-41.24, 20.64) * mm, "end": v(-46.74, 20.64) * mm});
            skLineSegment(sketch, "E8.14.0.6", {"start": v(-46.74, 20.64) * mm, "end": v(-49.5, 25.4) * mm});
            skLineSegment(sketch, "E8.17.0.6", {"start": v(-49.5, 25.4) * mm, "end": v(-46.74, 30.16) * mm});
            skLineSegment(sketch, "E8.0.0.7", {"start": v(-46.74, 42.86) * mm, "end": v(-41.24, 42.86) * mm});
            skLineSegment(sketch, "E8.3.0.7", {"start": v(-41.24, 42.86) * mm, "end": v(-38.5, 38.1) * mm});
            skLineSegment(sketch, "E8.6.0.7", {"start": v(-38.5, 38.1) * mm, "end": v(-41.24, 33.34) * mm});
            skCircle(sketch, "E8.9.0.7", {"center": v(-44, 38.1) * mm, "radius": 4.76 * mm, "construction": true});
            skLineSegment(sketch, "E8.11.0.7", {"start": v(-41.24, 33.34) * mm, "end": v(-46.74, 33.34) * mm});
            skLineSegment(sketch, "E8.14.0.7", {"start": v(-46.74, 33.34) * mm, "end": v(-49.5, 38.1) * mm});
            skLineSegment(sketch, "E8.17.0.7", {"start": v(-49.5, 38.1) * mm, "end": v(-46.74, 42.86) * mm});
            skLineSegment(sketch, "E8.0.1.4", {"start": v(-24.75, 4.76) * mm, "end": v(-19.25, 4.76) * mm});
            skLineSegment(sketch, "E8.3.1.4", {"start": v(-19.25, 4.76) * mm, "end": v(-16.5, 0) * mm});
            skLineSegment(sketch, "E8.6.1.4", {"start": v(-16.5, 0) * mm, "end": v(-19.25, -4.76) * mm});
            skCircle(sketch, "E8.9.1.4", {"center": v(-22, 0) * mm, "radius": 4.76 * mm, "construction": true});
            skLineSegment(sketch, "E8.11.1.4", {"start": v(-19.25, -4.76) * mm, "end": v(-24.75, -4.76) * mm});
            skLineSegment(sketch, "E8.14.1.4", {"start": v(-24.75, -4.76) * mm, "end": v(-27.5, 0) * mm});
            skLineSegment(sketch, "E8.17.1.4", {"start": v(-27.5, 0) * mm, "end": v(-24.75, 4.76) * mm});
            skLineSegment(sketch, "E8.0.1.5", {"start": v(-24.75, 17.46) * mm, "end": v(-19.25, 17.46) * mm});
            skLineSegment(sketch, "E8.3.1.5", {"start": v(-19.25, 17.46) * mm, "end": v(-16.5, 12.7) * mm});
            skLineSegment(sketch, "E8.6.1.5", {"start": v(-16.5, 12.7) * mm, "end": v(-19.25, 7.94) * mm});
            skCircle(sketch, "E8.9.1.5", {"center": v(-22, 12.7) * mm, "radius": 4.76 * mm, "construction": true});
            skLineSegment(sketch, "E8.11.1.5", {"start": v(-19.25, 7.94) * mm, "end": v(-24.75, 7.94) * mm});
            skLineSegment(sketch, "E8.14.1.5", {"start": v(-24.75, 7.94) * mm, "end": v(-27.5, 12.7) * mm});
            skLineSegment(sketch, "E8.17.1.5", {"start": v(-27.5, 12.7) * mm, "end": v(-24.75, 17.46) * mm});
            skLineSegment(sketch, "E8.0.1.6", {"start": v(-24.75, 30.16) * mm, "end": v(-19.25, 30.16) * mm});
            skLineSegment(sketch, "E8.3.1.6", {"start": v(-19.25, 30.16) * mm, "end": v(-16.5, 25.4) * mm});
            skLineSegment(sketch, "E8.6.1.6", {"start": v(-16.5, 25.4) * mm, "end": v(-19.25, 20.64) * mm});
            skCircle(sketch, "E8.9.1.6", {"center": v(-22, 25.4) * mm, "radius": 4.76 * mm, "construction": true});
            skLineSegment(sketch, "E8.11.1.6", {"start": v(-19.25, 20.64) * mm, "end": v(-24.75, 20.64) * mm});
            skLineSegment(sketch, "E8.14.1.6", {"start": v(-24.75, 20.64) * mm, "end": v(-27.5, 25.4) * mm});
            skLineSegment(sketch, "E8.17.1.6", {"start": v(-27.5, 25.4) * mm, "end": v(-24.75, 30.16) * mm});
            skLineSegment(sketch, "E8.0.1.7", {"start": v(-24.75, 42.86) * mm, "end": v(-19.25, 42.86) * mm});
            skLineSegment(sketch, "E8.3.1.7", {"start": v(-19.25, 42.86) * mm, "end": v(-16.5, 38.1) * mm});
            skLineSegment(sketch, "E8.6.1.7", {"start": v(-16.5, 38.1) * mm, "end": v(-19.25, 33.34) * mm});
            skCircle(sketch, "E8.9.1.7", {"center": v(-22, 38.1) * mm, "radius": 4.76 * mm, "construction": true});
            skLineSegment(sketch, "E8.11.1.7", {"start": v(-19.25, 33.34) * mm, "end": v(-24.75, 33.34) * mm});
            skLineSegment(sketch, "E8.14.1.7", {"start": v(-24.75, 33.34) * mm, "end": v(-27.5, 38.1) * mm});
            skLineSegment(sketch, "E8.17.1.7", {"start": v(-27.5, 38.1) * mm, "end": v(-24.75, 42.86) * mm});
            skLineSegment(sketch, "E8.0.2.4", {"start": v(-2.75, 4.76) * mm, "end": v(2.75, 4.76) * mm});
            skLineSegment(sketch, "E8.3.2.4", {"start": v(2.75, 4.76) * mm, "end": v(5.5, 0) * mm});
            skLineSegment(sketch, "E8.6.2.4", {"start": v(5.5, 0) * mm, "end": v(2.75, -4.76) * mm});
            skCircle(sketch, "E8.9.2.4", {"center": v(0, 0) * mm, "radius": 4.76 * mm, "construction": true});
            skLineSegment(sketch, "E8.11.2.4", {"start": v(2.75, -4.76) * mm, "end": v(-2.75, -4.76) * mm});
            skLineSegment(sketch, "E8.14.2.4", {"start": v(-2.75, -4.76) * mm, "end": v(-5.5, 0) * mm});
            skLineSegment(sketch, "E8.17.2.4", {"start": v(-5.5, 0) * mm, "end": v(-2.75, 4.76) * mm});
            skLineSegment(sketch, "E8.0.2.5", {"start": v(-2.75, 17.46) * mm, "end": v(2.75, 17.46) * mm});
            skLineSegment(sketch, "E8.3.2.5", {"start": v(2.75, 17.46) * mm, "end": v(5.5, 12.7) * mm});
            skLineSegment(sketch, "E8.6.2.5", {"start": v(5.5, 12.7) * mm, "end": v(2.75, 7.94) * mm});
            skCircle(sketch, "E8.9.2.5", {"center": v(0, 12.7) * mm, "radius": 4.76 * mm, "construction": true});
            skLineSegment(sketch, "E8.11.2.5", {"start": v(2.75, 7.94) * mm, "end": v(-2.75, 7.94) * mm});
            skLineSegment(sketch, "E8.14.2.5", {"start": v(-2.75, 7.94) * mm, "end": v(-5.5, 12.7) * mm});
            skLineSegment(sketch, "E8.17.2.5", {"start": v(-5.5, 12.7) * mm, "end": v(-2.75, 17.46) * mm});
            skLineSegment(sketch, "E8.0.2.6", {"start": v(-2.75, 30.16) * mm, "end": v(2.75, 30.16) * mm});
            skLineSegment(sketch, "E8.3.2.6", {"start": v(2.75, 30.16) * mm, "end": v(5.5, 25.4) * mm});
            skLineSegment(sketch, "E8.6.2.6", {"start": v(5.5, 25.4) * mm, "end": v(2.75, 20.64) * mm});
            skCircle(sketch, "E8.9.2.6", {"center": v(0, 25.4) * mm, "radius": 4.76 * mm, "construction": true});
            skLineSegment(sketch, "E8.11.2.6", {"start": v(2.75, 20.64) * mm, "end": v(-2.75, 20.64) * mm});
            skLineSegment(sketch, "E8.14.2.6", {"start": v(-2.75, 20.64) * mm, "end": v(-5.5, 25.4) * mm});
            skLineSegment(sketch, "E8.17.2.6", {"start": v(-5.5, 25.4) * mm, "end": v(-2.75, 30.16) * mm});
            skLineSegment(sketch, "E8.0.2.7", {"start": v(-2.75, 42.86) * mm, "end": v(2.75, 42.86) * mm});
            skLineSegment(sketch, "E8.3.2.7", {"start": v(2.75, 42.86) * mm, "end": v(5.5, 38.1) * mm});
            skLineSegment(sketch, "E8.6.2.7", {"start": v(5.5, 38.1) * mm, "end": v(2.75, 33.34) * mm});
            skCircle(sketch, "E8.9.2.7", {"center": v(0, 38.1) * mm, "radius": 4.76 * mm, "construction": true});
            skLineSegment(sketch, "E8.11.2.7", {"start": v(2.75, 33.34) * mm, "end": v(-2.75, 33.34) * mm});
            skLineSegment(sketch, "E8.14.2.7", {"start": v(-2.75, 33.34) * mm, "end": v(-5.5, 38.1) * mm});
            skLineSegment(sketch, "E8.17.2.7", {"start": v(-5.5, 38.1) * mm, "end": v(-2.75, 42.86) * mm});
            skLineSegment(sketch, "E8.0.3.4", {"start": v(19.25, 4.76) * mm, "end": v(24.75, 4.76) * mm});
            skLineSegment(sketch, "E8.3.3.4", {"start": v(24.75, 4.76) * mm, "end": v(27.5, 0) * mm});
            skLineSegment(sketch, "E8.6.3.4", {"start": v(27.5, 0) * mm, "end": v(24.75, -4.76) * mm});
            skCircle(sketch, "E8.9.3.4", {"center": v(22, 0) * mm, "radius": 4.76 * mm, "construction": true});
            skLineSegment(sketch, "E8.11.3.4", {"start": v(24.75, -4.76) * mm, "end": v(19.25, -4.76) * mm});
            skLineSegment(sketch, "E8.14.3.4", {"start": v(19.25, -4.76) * mm, "end": v(16.5, 0) * mm});
            skLineSegment(sketch, "E8.17.3.4", {"start": v(16.5, 0) * mm, "end": v(19.25, 4.76) * mm});
            skLineSegment(sketch, "E8.0.3.5", {"start": v(19.25, 17.46) * mm, "end": v(24.75, 17.46) * mm});
            skLineSegment(sketch, "E8.3.3.5", {"start": v(24.75, 17.46) * mm, "end": v(27.5, 12.7) * mm});
            skLineSegment(sketch, "E8.6.3.5", {"start": v(27.5, 12.7) * mm, "end": v(24.75, 7.94) * mm});
            skCircle(sketch, "E8.9.3.5", {"center": v(22, 12.7) * mm, "radius": 4.76 * mm, "construction": true});
            skLineSegment(sketch, "E8.11.3.5", {"start": v(24.75, 7.94) * mm, "end": v(19.25, 7.94) * mm});
            skLineSegment(sketch, "E8.14.3.5", {"start": v(19.25, 7.94) * mm, "end": v(16.5, 12.7) * mm});
            skLineSegment(sketch, "E8.17.3.5", {"start": v(16.5, 12.7) * mm, "end": v(19.25, 17.46) * mm});
            skLineSegment(sketch, "E8.0.3.6", {"start": v(19.25, 30.16) * mm, "end": v(24.75, 30.16) * mm});
            skLineSegment(sketch, "E8.3.3.6", {"start": v(24.75, 30.16) * mm, "end": v(27.5, 25.4) * mm});
            skLineSegment(sketch, "E8.6.3.6", {"start": v(27.5, 25.4) * mm, "end": v(24.75, 20.64) * mm});
            skCircle(sketch, "E8.9.3.6", {"center": v(22, 25.4) * mm, "radius": 4.76 * mm, "construction": true});
            skLineSegment(sketch, "E8.11.3.6", {"start": v(24.75, 20.64) * mm, "end": v(19.25, 20.64) * mm});
            skLineSegment(sketch, "E8.14.3.6", {"start": v(19.25, 20.64) * mm, "end": v(16.5, 25.4) * mm});
            skLineSegment(sketch, "E8.17.3.6", {"start": v(16.5, 25.4) * mm, "end": v(19.25, 30.16) * mm});
            skLineSegment(sketch, "E8.0.3.7", {"start": v(19.25, 42.86) * mm, "end": v(24.75, 42.86) * mm});
            skLineSegment(sketch, "E8.3.3.7", {"start": v(24.75, 42.86) * mm, "end": v(27.5, 38.1) * mm});
            skLineSegment(sketch, "E8.6.3.7", {"start": v(27.5, 38.1) * mm, "end": v(24.75, 33.34) * mm});
            skCircle(sketch, "E8.9.3.7", {"center": v(22, 38.1) * mm, "radius": 4.76 * mm, "construction": true});
            skLineSegment(sketch, "E8.11.3.7", {"start": v(24.75, 33.34) * mm, "end": v(19.25, 33.34) * mm});
            skLineSegment(sketch, "E8.14.3.7", {"start": v(19.25, 33.34) * mm, "end": v(16.5, 38.1) * mm});
            skLineSegment(sketch, "E8.17.3.7", {"start": v(16.5, 38.1) * mm, "end": v(19.25, 42.86) * mm});
            skLineSegment(sketch, "E8.0.4.4", {"start": v(41.24, 4.76) * mm, "end": v(46.74, 4.76) * mm});
            skLineSegment(sketch, "E8.3.4.4", {"start": v(46.74, 4.76) * mm, "end": v(49.5, 0) * mm});
            skLineSegment(sketch, "E8.6.4.4", {"start": v(49.5, 0) * mm, "end": v(46.74, -4.76) * mm});
            skCircle(sketch, "E8.9.4.4", {"center": v(44, 0) * mm, "radius": 4.76 * mm, "construction": true});
            skLineSegment(sketch, "E8.11.4.4", {"start": v(46.74, -4.76) * mm, "end": v(41.24, -4.76) * mm});
            skLineSegment(sketch, "E8.14.4.4", {"start": v(41.24, -4.76) * mm, "end": v(38.5, 0) * mm});
            skLineSegment(sketch, "E8.17.4.4", {"start": v(38.5, 0) * mm, "end": v(41.24, 4.76) * mm});
            skLineSegment(sketch, "E8.0.4.5", {"start": v(41.24, 17.46) * mm, "end": v(46.74, 17.46) * mm});
            skLineSegment(sketch, "E8.3.4.5", {"start": v(46.74, 17.46) * mm, "end": v(49.5, 12.7) * mm});
            skLineSegment(sketch, "E8.6.4.5", {"start": v(49.5, 12.7) * mm, "end": v(46.74, 7.94) * mm});
            skCircle(sketch, "E8.9.4.5", {"center": v(44, 12.7) * mm, "radius": 4.76 * mm, "construction": true});
            skLineSegment(sketch, "E8.11.4.5", {"start": v(46.74, 7.94) * mm, "end": v(41.24, 7.94) * mm});
            skLineSegment(sketch, "E8.14.4.5", {"start": v(41.24, 7.94) * mm, "end": v(38.5, 12.7) * mm});
            skLineSegment(sketch, "E8.17.4.5", {"start": v(38.5, 12.7) * mm, "end": v(41.24, 17.46) * mm});
            skLineSegment(sketch, "E8.0.4.6", {"start": v(41.24, 30.16) * mm, "end": v(46.74, 30.16) * mm});
            skLineSegment(sketch, "E8.3.4.6", {"start": v(46.74, 30.16) * mm, "end": v(49.5, 25.4) * mm});
            skLineSegment(sketch, "E8.6.4.6", {"start": v(49.5, 25.4) * mm, "end": v(46.74, 20.64) * mm});
            skCircle(sketch, "E8.9.4.6", {"center": v(44, 25.4) * mm, "radius": 4.76 * mm, "construction": true});
            skLineSegment(sketch, "E8.11.4.6", {"start": v(46.74, 20.64) * mm, "end": v(41.24, 20.64) * mm});
            skLineSegment(sketch, "E8.14.4.6", {"start": v(41.24, 20.64) * mm, "end": v(38.5, 25.4) * mm});
            skLineSegment(sketch, "E8.17.4.6", {"start": v(38.5, 25.4) * mm, "end": v(41.24, 30.16) * mm});
            skLineSegment(sketch, "E8.0.4.7", {"start": v(41.24, 42.86) * mm, "end": v(46.74, 42.86) * mm});
            skLineSegment(sketch, "E8.3.4.7", {"start": v(46.74, 42.86) * mm, "end": v(49.5, 38.1) * mm});
            skLineSegment(sketch, "E8.6.4.7", {"start": v(49.5, 38.1) * mm, "end": v(46.74, 33.34) * mm});
            skCircle(sketch, "E8.9.4.7", {"center": v(44, 38.1) * mm, "radius": 4.76 * mm, "construction": true});
            skLineSegment(sketch, "E8.11.4.7", {"start": v(46.74, 33.34) * mm, "end": v(41.24, 33.34) * mm});
            skLineSegment(sketch, "E8.14.4.7", {"start": v(41.24, 33.34) * mm, "end": v(38.5, 38.1) * mm});
            skLineSegment(sketch, "E8.17.4.7", {"start": v(38.5, 38.1) * mm, "end": v(41.24, 42.86) * mm});
            skLineSegment(sketch, "E8.0.5.4", {"start": v(63.24, 4.76) * mm, "end": v(68.74, 4.76) * mm});
            skLineSegment(sketch, "E8.3.5.4", {"start": v(68.74, 4.76) * mm, "end": v(71.49, 0) * mm});
            skLineSegment(sketch, "E8.6.5.4", {"start": v(71.49, 0) * mm, "end": v(68.74, -4.76) * mm});
            skCircle(sketch, "E8.9.5.4", {"center": v(65.99, 0) * mm, "radius": 4.76 * mm, "construction": true});
            skLineSegment(sketch, "E8.11.5.4", {"start": v(68.74, -4.76) * mm, "end": v(63.24, -4.76) * mm});
            skLineSegment(sketch, "E8.14.5.4", {"start": v(63.24, -4.76) * mm, "end": v(60.49, 0) * mm});
            skLineSegment(sketch, "E8.17.5.4", {"start": v(60.49, 0) * mm, "end": v(63.24, 4.76) * mm});
            skLineSegment(sketch, "E8.0.5.5", {"start": v(63.24, 17.46) * mm, "end": v(68.74, 17.46) * mm});
            skLineSegment(sketch, "E8.3.5.5", {"start": v(68.74, 17.46) * mm, "end": v(71.49, 12.7) * mm});
            skLineSegment(sketch, "E8.6.5.5", {"start": v(71.49, 12.7) * mm, "end": v(68.74, 7.94) * mm});
            skCircle(sketch, "E8.9.5.5", {"center": v(65.99, 12.7) * mm, "radius": 4.76 * mm, "construction": true});
            skLineSegment(sketch, "E8.11.5.5", {"start": v(68.74, 7.94) * mm, "end": v(63.24, 7.94) * mm});
            skLineSegment(sketch, "E8.14.5.5", {"start": v(63.24, 7.94) * mm, "end": v(60.49, 12.7) * mm});
            skLineSegment(sketch, "E8.17.5.5", {"start": v(60.49, 12.7) * mm, "end": v(63.24, 17.46) * mm});
            skLineSegment(sketch, "E8.0.5.6", {"start": v(63.24, 30.16) * mm, "end": v(68.74, 30.16) * mm});
            skLineSegment(sketch, "E8.3.5.6", {"start": v(68.74, 30.16) * mm, "end": v(71.49, 25.4) * mm});
            skLineSegment(sketch, "E8.6.5.6", {"start": v(71.49, 25.4) * mm, "end": v(68.74, 20.64) * mm});
            skCircle(sketch, "E8.9.5.6", {"center": v(65.99, 25.4) * mm, "radius": 4.76 * mm, "construction": true});
            skLineSegment(sketch, "E8.11.5.6", {"start": v(68.74, 20.64) * mm, "end": v(63.24, 20.64) * mm});
            skLineSegment(sketch, "E8.14.5.6", {"start": v(63.24, 20.64) * mm, "end": v(60.49, 25.4) * mm});
            skLineSegment(sketch, "E8.17.5.6", {"start": v(60.49, 25.4) * mm, "end": v(63.24, 30.16) * mm});
            skLineSegment(sketch, "E8.0.5.7", {"start": v(63.24, 42.86) * mm, "end": v(68.74, 42.86) * mm});
            skLineSegment(sketch, "E8.3.5.7", {"start": v(68.74, 42.86) * mm, "end": v(71.49, 38.1) * mm});
            skLineSegment(sketch, "E8.6.5.7", {"start": v(71.49, 38.1) * mm, "end": v(68.74, 33.34) * mm});
            skCircle(sketch, "E8.9.5.7", {"center": v(65.99, 38.1) * mm, "radius": 4.76 * mm, "construction": true});
            skLineSegment(sketch, "E8.11.5.7", {"start": v(68.74, 33.34) * mm, "end": v(63.24, 33.34) * mm});
            skLineSegment(sketch, "E8.14.5.7", {"start": v(63.24, 33.34) * mm, "end": v(60.49, 38.1) * mm});
            skLineSegment(sketch, "E8.17.5.7", {"start": v(60.49, 38.1) * mm, "end": v(63.24, 42.86) * mm});
            skCircle(sketch, "E9.0.0.4", {"center": v(-33, 6.35) * mm, "radius": 4.76 * mm, "construction": true});
            skLineSegment(sketch, "E9.2.0.4", {"start": v(-38.5, 6.35) * mm, "end": v(-35.74, 11.11) * mm});
            skLineSegment(sketch, "E9.5.0.4", {"start": v(-35.74, 11.11) * mm, "end": v(-30.24, 11.11) * mm});
            skLineSegment(sketch, "E9.8.0.4", {"start": v(-30.24, 11.11) * mm, "end": v(-27.5, 6.35) * mm});
            skLineSegment(sketch, "E9.11.0.4", {"start": v(-27.5, 6.35) * mm, "end": v(-30.24, 1.59) * mm});
            skLineSegment(sketch, "E9.14.0.4", {"start": v(-30.24, 1.59) * mm, "end": v(-35.74, 1.59) * mm});
            skLineSegment(sketch, "E9.17.0.4", {"start": v(-35.74, 1.59) * mm, "end": v(-38.5, 6.35) * mm});
            skCircle(sketch, "E9.0.0.5", {"center": v(-33, 19.05) * mm, "radius": 4.76 * mm, "construction": true});
            skLineSegment(sketch, "E9.2.0.5", {"start": v(-38.5, 19.05) * mm, "end": v(-35.74, 23.81) * mm});
            skLineSegment(sketch, "E9.5.0.5", {"start": v(-35.74, 23.81) * mm, "end": v(-30.24, 23.81) * mm});
            skLineSegment(sketch, "E9.8.0.5", {"start": v(-30.24, 23.81) * mm, "end": v(-27.5, 19.05) * mm});
            skLineSegment(sketch, "E9.11.0.5", {"start": v(-27.5, 19.05) * mm, "end": v(-30.24, 14.29) * mm});
            skLineSegment(sketch, "E9.14.0.5", {"start": v(-30.24, 14.29) * mm, "end": v(-35.74, 14.29) * mm});
            skLineSegment(sketch, "E9.17.0.5", {"start": v(-35.74, 14.29) * mm, "end": v(-38.5, 19.05) * mm});
            skCircle(sketch, "E9.0.0.6", {"center": v(-33, 31.75) * mm, "radius": 4.76 * mm, "construction": true});
            skLineSegment(sketch, "E9.2.0.6", {"start": v(-38.5, 31.75) * mm, "end": v(-35.74, 36.51) * mm});
            skLineSegment(sketch, "E9.5.0.6", {"start": v(-35.74, 36.51) * mm, "end": v(-30.24, 36.51) * mm});
            skLineSegment(sketch, "E9.8.0.6", {"start": v(-30.24, 36.51) * mm, "end": v(-27.5, 31.75) * mm});
            skLineSegment(sketch, "E9.11.0.6", {"start": v(-27.5, 31.75) * mm, "end": v(-30.24, 26.99) * mm});
            skLineSegment(sketch, "E9.14.0.6", {"start": v(-30.24, 26.99) * mm, "end": v(-35.74, 26.99) * mm});
            skLineSegment(sketch, "E9.17.0.6", {"start": v(-35.74, 26.99) * mm, "end": v(-38.5, 31.75) * mm});
            skCircle(sketch, "E9.0.1.4", {"center": v(-11, 6.35) * mm, "radius": 4.76 * mm, "construction": true});
            skLineSegment(sketch, "E9.2.1.4", {"start": v(-16.5, 6.35) * mm, "end": v(-13.75, 11.11) * mm});
            skLineSegment(sketch, "E9.5.1.4", {"start": v(-13.75, 11.11) * mm, "end": v(-8.25, 11.11) * mm});
            skLineSegment(sketch, "E9.8.1.4", {"start": v(-8.25, 11.11) * mm, "end": v(-5.5, 6.35) * mm});
            skLineSegment(sketch, "E9.11.1.4", {"start": v(-5.5, 6.35) * mm, "end": v(-8.25, 1.59) * mm});
            skLineSegment(sketch, "E9.14.1.4", {"start": v(-8.25, 1.59) * mm, "end": v(-13.75, 1.59) * mm});
            skLineSegment(sketch, "E9.17.1.4", {"start": v(-13.75, 1.59) * mm, "end": v(-16.5, 6.35) * mm});
            skCircle(sketch, "E9.0.1.5", {"center": v(-11, 19.05) * mm, "radius": 4.76 * mm, "construction": true});
            skLineSegment(sketch, "E9.2.1.5", {"start": v(-16.5, 19.05) * mm, "end": v(-13.75, 23.81) * mm});
            skLineSegment(sketch, "E9.5.1.5", {"start": v(-13.75, 23.81) * mm, "end": v(-8.25, 23.81) * mm});
            skLineSegment(sketch, "E9.8.1.5", {"start": v(-8.25, 23.81) * mm, "end": v(-5.5, 19.05) * mm});
            skLineSegment(sketch, "E9.11.1.5", {"start": v(-5.5, 19.05) * mm, "end": v(-8.25, 14.29) * mm});
            skLineSegment(sketch, "E9.14.1.5", {"start": v(-8.25, 14.29) * mm, "end": v(-13.75, 14.29) * mm});
            skLineSegment(sketch, "E9.17.1.5", {"start": v(-13.75, 14.29) * mm, "end": v(-16.5, 19.05) * mm});
            skCircle(sketch, "E9.0.1.6", {"center": v(-11, 31.75) * mm, "radius": 4.76 * mm, "construction": true});
            skLineSegment(sketch, "E9.2.1.6", {"start": v(-16.5, 31.75) * mm, "end": v(-13.75, 36.51) * mm});
            skLineSegment(sketch, "E9.5.1.6", {"start": v(-13.75, 36.51) * mm, "end": v(-8.25, 36.51) * mm});
            skLineSegment(sketch, "E9.8.1.6", {"start": v(-8.25, 36.51) * mm, "end": v(-5.5, 31.75) * mm});
            skLineSegment(sketch, "E9.11.1.6", {"start": v(-5.5, 31.75) * mm, "end": v(-8.25, 26.99) * mm});
            skLineSegment(sketch, "E9.14.1.6", {"start": v(-8.25, 26.99) * mm, "end": v(-13.75, 26.99) * mm});
            skLineSegment(sketch, "E9.17.1.6", {"start": v(-13.75, 26.99) * mm, "end": v(-16.5, 31.75) * mm});
            skCircle(sketch, "E9.0.2.4", {"center": v(11, 6.35) * mm, "radius": 4.76 * mm, "construction": true});
            skLineSegment(sketch, "E9.2.2.4", {"start": v(5.5, 6.35) * mm, "end": v(8.25, 11.11) * mm});
            skLineSegment(sketch, "E9.5.2.4", {"start": v(8.25, 11.11) * mm, "end": v(13.75, 11.11) * mm});
            skLineSegment(sketch, "E9.8.2.4", {"start": v(13.75, 11.11) * mm, "end": v(16.5, 6.35) * mm});
            skLineSegment(sketch, "E9.11.2.4", {"start": v(16.5, 6.35) * mm, "end": v(13.75, 1.59) * mm});
            skLineSegment(sketch, "E9.14.2.4", {"start": v(13.75, 1.59) * mm, "end": v(8.25, 1.59) * mm});
            skLineSegment(sketch, "E9.17.2.4", {"start": v(8.25, 1.59) * mm, "end": v(5.5, 6.35) * mm});
            skCircle(sketch, "E9.0.2.5", {"center": v(11, 19.05) * mm, "radius": 4.76 * mm, "construction": true});
            skLineSegment(sketch, "E9.2.2.5", {"start": v(5.5, 19.05) * mm, "end": v(8.25, 23.81) * mm});
            skLineSegment(sketch, "E9.5.2.5", {"start": v(8.25, 23.81) * mm, "end": v(13.75, 23.81) * mm});
            skLineSegment(sketch, "E9.8.2.5", {"start": v(13.75, 23.81) * mm, "end": v(16.5, 19.05) * mm});
            skLineSegment(sketch, "E9.11.2.5", {"start": v(16.5, 19.05) * mm, "end": v(13.75, 14.29) * mm});
            skLineSegment(sketch, "E9.14.2.5", {"start": v(13.75, 14.29) * mm, "end": v(8.25, 14.29) * mm});
            skLineSegment(sketch, "E9.17.2.5", {"start": v(8.25, 14.29) * mm, "end": v(5.5, 19.05) * mm});
            skCircle(sketch, "E9.0.2.6", {"center": v(11, 31.75) * mm, "radius": 4.76 * mm, "construction": true});
            skLineSegment(sketch, "E9.2.2.6", {"start": v(5.5, 31.75) * mm, "end": v(8.25, 36.51) * mm});
            skLineSegment(sketch, "E9.5.2.6", {"start": v(8.25, 36.51) * mm, "end": v(13.75, 36.51) * mm});
            skLineSegment(sketch, "E9.8.2.6", {"start": v(13.75, 36.51) * mm, "end": v(16.5, 31.75) * mm});
            skLineSegment(sketch, "E9.11.2.6", {"start": v(16.5, 31.75) * mm, "end": v(13.75, 26.99) * mm});
            skLineSegment(sketch, "E9.14.2.6", {"start": v(13.75, 26.99) * mm, "end": v(8.25, 26.99) * mm});
            skLineSegment(sketch, "E9.17.2.6", {"start": v(8.25, 26.99) * mm, "end": v(5.5, 31.75) * mm});
            skCircle(sketch, "E9.0.3.4", {"center": v(33, 6.35) * mm, "radius": 4.76 * mm, "construction": true});
            skLineSegment(sketch, "E9.2.3.4", {"start": v(27.5, 6.35) * mm, "end": v(30.25, 11.11) * mm});
            skLineSegment(sketch, "E9.5.3.4", {"start": v(30.25, 11.11) * mm, "end": v(35.74, 11.11) * mm});
            skLineSegment(sketch, "E9.8.3.4", {"start": v(35.74, 11.11) * mm, "end": v(38.5, 6.35) * mm});
            skLineSegment(sketch, "E9.11.3.4", {"start": v(38.5, 6.35) * mm, "end": v(35.74, 1.59) * mm});
            skLineSegment(sketch, "E9.14.3.4", {"start": v(35.74, 1.59) * mm, "end": v(30.25, 1.59) * mm});
            skLineSegment(sketch, "E9.17.3.4", {"start": v(30.25, 1.59) * mm, "end": v(27.5, 6.35) * mm});
            skCircle(sketch, "E9.0.3.5", {"center": v(33, 19.05) * mm, "radius": 4.76 * mm, "construction": true});
            skLineSegment(sketch, "E9.2.3.5", {"start": v(27.5, 19.05) * mm, "end": v(30.25, 23.81) * mm});
            skLineSegment(sketch, "E9.5.3.5", {"start": v(30.25, 23.81) * mm, "end": v(35.74, 23.81) * mm});
            skLineSegment(sketch, "E9.8.3.5", {"start": v(35.74, 23.81) * mm, "end": v(38.5, 19.05) * mm});
            skLineSegment(sketch, "E9.11.3.5", {"start": v(38.5, 19.05) * mm, "end": v(35.74, 14.29) * mm});
            skLineSegment(sketch, "E9.14.3.5", {"start": v(35.74, 14.29) * mm, "end": v(30.25, 14.29) * mm});
            skLineSegment(sketch, "E9.17.3.5", {"start": v(30.25, 14.29) * mm, "end": v(27.5, 19.05) * mm});
            skCircle(sketch, "E9.0.3.6", {"center": v(33, 31.75) * mm, "radius": 4.76 * mm, "construction": true});
            skLineSegment(sketch, "E9.2.3.6", {"start": v(27.5, 31.75) * mm, "end": v(30.25, 36.51) * mm});
            skLineSegment(sketch, "E9.5.3.6", {"start": v(30.25, 36.51) * mm, "end": v(35.74, 36.51) * mm});
            skLineSegment(sketch, "E9.8.3.6", {"start": v(35.74, 36.51) * mm, "end": v(38.5, 31.75) * mm});
            skLineSegment(sketch, "E9.11.3.6", {"start": v(38.5, 31.75) * mm, "end": v(35.74, 26.99) * mm});
            skLineSegment(sketch, "E9.14.3.6", {"start": v(35.74, 26.99) * mm, "end": v(30.25, 26.99) * mm});
            skLineSegment(sketch, "E9.17.3.6", {"start": v(30.25, 26.99) * mm, "end": v(27.5, 31.75) * mm});
            skCircle(sketch, "E9.0.4.4", {"center": v(55, 6.35) * mm, "radius": 4.76 * mm, "construction": true});
            skLineSegment(sketch, "E9.2.4.4", {"start": v(49.5, 6.35) * mm, "end": v(52.24, 11.11) * mm});
            skLineSegment(sketch, "E9.5.4.4", {"start": v(52.24, 11.11) * mm, "end": v(57.74, 11.11) * mm});
            skLineSegment(sketch, "E9.8.4.4", {"start": v(57.74, 11.11) * mm, "end": v(60.5, 6.35) * mm});
            skLineSegment(sketch, "E9.11.4.4", {"start": v(60.5, 6.35) * mm, "end": v(57.74, 1.59) * mm});
            skLineSegment(sketch, "E9.14.4.4", {"start": v(57.74, 1.59) * mm, "end": v(52.24, 1.59) * mm});
            skLineSegment(sketch, "E9.17.4.4", {"start": v(52.24, 1.59) * mm, "end": v(49.5, 6.35) * mm});
            skCircle(sketch, "E9.0.4.5", {"center": v(55, 19.05) * mm, "radius": 4.76 * mm, "construction": true});
            skLineSegment(sketch, "E9.2.4.5", {"start": v(49.5, 19.05) * mm, "end": v(52.24, 23.81) * mm});
            skLineSegment(sketch, "E9.5.4.5", {"start": v(52.24, 23.81) * mm, "end": v(57.74, 23.81) * mm});
            skLineSegment(sketch, "E9.8.4.5", {"start": v(57.74, 23.81) * mm, "end": v(60.5, 19.05) * mm});
            skLineSegment(sketch, "E9.11.4.5", {"start": v(60.5, 19.05) * mm, "end": v(57.74, 14.29) * mm});
            skLineSegment(sketch, "E9.14.4.5", {"start": v(57.74, 14.29) * mm, "end": v(52.24, 14.29) * mm});
            skLineSegment(sketch, "E9.17.4.5", {"start": v(52.24, 14.29) * mm, "end": v(49.5, 19.05) * mm});
            skCircle(sketch, "E9.0.4.6", {"center": v(55, 31.75) * mm, "radius": 4.76 * mm, "construction": true});
            skLineSegment(sketch, "E9.2.4.6", {"start": v(49.5, 31.75) * mm, "end": v(52.24, 36.51) * mm});
            skLineSegment(sketch, "E9.5.4.6", {"start": v(52.24, 36.51) * mm, "end": v(57.74, 36.51) * mm});
            skLineSegment(sketch, "E9.8.4.6", {"start": v(57.74, 36.51) * mm, "end": v(60.5, 31.75) * mm});
            skLineSegment(sketch, "E9.11.4.6", {"start": v(60.5, 31.75) * mm, "end": v(57.74, 26.99) * mm});
            skLineSegment(sketch, "E9.14.4.6", {"start": v(57.74, 26.99) * mm, "end": v(52.24, 26.99) * mm});
            skLineSegment(sketch, "E9.17.4.6", {"start": v(52.24, 26.99) * mm, "end": v(49.5, 31.75) * mm});
            skCircle(sketch, "E10.0.0.7", {"center": v(-33, 44.45) * mm, "radius": 4.76 * mm, "construction": true});
            skLineSegment(sketch, "E10.2.0.7", {"start": v(-38.5, 44.45) * mm, "end": v(-35.74, 49.21) * mm});
            skLineSegment(sketch, "E10.5.0.7", {"start": v(-35.74, 49.21) * mm, "end": v(-30.24, 49.21) * mm});
            skLineSegment(sketch, "E10.8.0.7", {"start": v(-30.24, 49.21) * mm, "end": v(-27.5, 44.45) * mm});
            skLineSegment(sketch, "E10.11.0.7", {"start": v(-27.5, 44.45) * mm, "end": v(-30.24, 39.69) * mm});
            skLineSegment(sketch, "E10.14.0.7", {"start": v(-30.24, 39.69) * mm, "end": v(-35.74, 39.69) * mm});
            skLineSegment(sketch, "E10.17.0.7", {"start": v(-35.74, 39.69) * mm, "end": v(-38.5, 44.45) * mm});
            skCircle(sketch, "E10.0.1.7", {"center": v(-11, 44.45) * mm, "radius": 4.76 * mm, "construction": true});
            skLineSegment(sketch, "E10.2.1.7", {"start": v(-16.5, 44.45) * mm, "end": v(-13.75, 49.21) * mm});
            skLineSegment(sketch, "E10.5.1.7", {"start": v(-13.75, 49.21) * mm, "end": v(-8.25, 49.21) * mm});
            skLineSegment(sketch, "E10.8.1.7", {"start": v(-8.25, 49.21) * mm, "end": v(-5.5, 44.45) * mm});
            skLineSegment(sketch, "E10.11.1.7", {"start": v(-5.5, 44.45) * mm, "end": v(-8.25, 39.69) * mm});
            skLineSegment(sketch, "E10.14.1.7", {"start": v(-8.25, 39.69) * mm, "end": v(-13.75, 39.69) * mm});
            skLineSegment(sketch, "E10.17.1.7", {"start": v(-13.75, 39.69) * mm, "end": v(-16.5, 44.45) * mm});
            skCircle(sketch, "E10.0.2.7", {"center": v(11, 44.45) * mm, "radius": 4.76 * mm, "construction": true});
            skLineSegment(sketch, "E10.2.2.7", {"start": v(5.5, 44.45) * mm, "end": v(8.25, 49.21) * mm});
            skLineSegment(sketch, "E10.5.2.7", {"start": v(8.25, 49.21) * mm, "end": v(13.75, 49.21) * mm});
            skLineSegment(sketch, "E10.8.2.7", {"start": v(13.75, 49.21) * mm, "end": v(16.5, 44.45) * mm});
            skLineSegment(sketch, "E10.11.2.7", {"start": v(16.5, 44.45) * mm, "end": v(13.75, 39.69) * mm});
            skLineSegment(sketch, "E10.14.2.7", {"start": v(13.75, 39.69) * mm, "end": v(8.25, 39.69) * mm});
            skLineSegment(sketch, "E10.17.2.7", {"start": v(8.25, 39.69) * mm, "end": v(5.5, 44.45) * mm});
            skCircle(sketch, "E10.0.3.7", {"center": v(33, 44.45) * mm, "radius": 4.76 * mm, "construction": true});
            skLineSegment(sketch, "E10.2.3.7", {"start": v(27.5, 44.45) * mm, "end": v(30.25, 49.21) * mm});
            skLineSegment(sketch, "E10.5.3.7", {"start": v(30.25, 49.21) * mm, "end": v(35.74, 49.21) * mm});
            skLineSegment(sketch, "E10.8.3.7", {"start": v(35.74, 49.21) * mm, "end": v(38.5, 44.45) * mm});
            skLineSegment(sketch, "E10.11.3.7", {"start": v(38.5, 44.45) * mm, "end": v(35.74, 39.69) * mm});
            skLineSegment(sketch, "E10.14.3.7", {"start": v(35.74, 39.69) * mm, "end": v(30.25, 39.69) * mm});
            skLineSegment(sketch, "E10.17.3.7", {"start": v(30.25, 39.69) * mm, "end": v(27.5, 44.45) * mm});
            skCircle(sketch, "E10.0.4.7", {"center": v(55, 44.45) * mm, "radius": 4.76 * mm, "construction": true});
            skLineSegment(sketch, "E10.2.4.7", {"start": v(49.5, 44.45) * mm, "end": v(52.24, 49.21) * mm});
            skLineSegment(sketch, "E10.5.4.7", {"start": v(52.24, 49.21) * mm, "end": v(57.74, 49.21) * mm});
            skLineSegment(sketch, "E10.8.4.7", {"start": v(57.74, 49.21) * mm, "end": v(60.5, 44.45) * mm});
            skLineSegment(sketch, "E10.11.4.7", {"start": v(60.5, 44.45) * mm, "end": v(57.74, 39.69) * mm});
            skLineSegment(sketch, "E10.14.4.7", {"start": v(57.74, 39.69) * mm, "end": v(52.24, 39.69) * mm});
            skLineSegment(sketch, "E10.17.4.7", {"start": v(52.24, 39.69) * mm, "end": v(49.5, 44.45) * mm});
            skLineSegment(sketch, "E11.0.0.8", {"start": v(-46.74, 55.56) * mm, "end": v(-41.24, 55.56) * mm});
            skLineSegment(sketch, "E11.3.0.8", {"start": v(-41.24, 55.56) * mm, "end": v(-38.5, 50.8) * mm});
            skLineSegment(sketch, "E11.6.0.8", {"start": v(-38.5, 50.8) * mm, "end": v(-41.24, 46.04) * mm});
            skCircle(sketch, "E11.9.0.8", {"center": v(-44, 50.8) * mm, "radius": 4.76 * mm, "construction": true});
            skLineSegment(sketch, "E11.11.0.8", {"start": v(-41.24, 46.04) * mm, "end": v(-46.74, 46.04) * mm});
            skLineSegment(sketch, "E11.14.0.8", {"start": v(-46.74, 46.04) * mm, "end": v(-49.5, 50.8) * mm});
            skLineSegment(sketch, "E11.17.0.8", {"start": v(-49.5, 50.8) * mm, "end": v(-46.74, 55.56) * mm});
            skLineSegment(sketch, "E11.0.1.8", {"start": v(-24.75, 55.56) * mm, "end": v(-19.25, 55.56) * mm});
            skLineSegment(sketch, "E11.3.1.8", {"start": v(-19.25, 55.56) * mm, "end": v(-16.5, 50.8) * mm});
            skLineSegment(sketch, "E11.6.1.8", {"start": v(-16.5, 50.8) * mm, "end": v(-19.25, 46.04) * mm});
            skCircle(sketch, "E11.9.1.8", {"center": v(-22, 50.8) * mm, "radius": 4.76 * mm, "construction": true});
            skLineSegment(sketch, "E11.11.1.8", {"start": v(-19.25, 46.04) * mm, "end": v(-24.75, 46.04) * mm});
            skLineSegment(sketch, "E11.14.1.8", {"start": v(-24.75, 46.04) * mm, "end": v(-27.5, 50.8) * mm});
            skLineSegment(sketch, "E11.17.1.8", {"start": v(-27.5, 50.8) * mm, "end": v(-24.75, 55.56) * mm});
            skLineSegment(sketch, "E11.0.2.8", {"start": v(-2.75, 55.56) * mm, "end": v(2.75, 55.56) * mm});
            skLineSegment(sketch, "E11.3.2.8", {"start": v(2.75, 55.56) * mm, "end": v(5.5, 50.8) * mm});
            skLineSegment(sketch, "E11.6.2.8", {"start": v(5.5, 50.8) * mm, "end": v(2.75, 46.04) * mm});
            skCircle(sketch, "E11.9.2.8", {"center": v(0, 50.8) * mm, "radius": 4.76 * mm, "construction": true});
            skLineSegment(sketch, "E11.11.2.8", {"start": v(2.75, 46.04) * mm, "end": v(-2.75, 46.04) * mm});
            skLineSegment(sketch, "E11.14.2.8", {"start": v(-2.75, 46.04) * mm, "end": v(-5.5, 50.8) * mm});
            skLineSegment(sketch, "E11.17.2.8", {"start": v(-5.5, 50.8) * mm, "end": v(-2.75, 55.56) * mm});
            skLineSegment(sketch, "E11.0.3.8", {"start": v(19.25, 55.56) * mm, "end": v(24.75, 55.56) * mm});
            skLineSegment(sketch, "E11.3.3.8", {"start": v(24.75, 55.56) * mm, "end": v(27.5, 50.8) * mm});
            skLineSegment(sketch, "E11.6.3.8", {"start": v(27.5, 50.8) * mm, "end": v(24.75, 46.04) * mm});
            skCircle(sketch, "E11.9.3.8", {"center": v(22, 50.8) * mm, "radius": 4.76 * mm, "construction": true});
            skLineSegment(sketch, "E11.11.3.8", {"start": v(24.75, 46.04) * mm, "end": v(19.25, 46.04) * mm});
            skLineSegment(sketch, "E11.14.3.8", {"start": v(19.25, 46.04) * mm, "end": v(16.5, 50.8) * mm});
            skLineSegment(sketch, "E11.17.3.8", {"start": v(16.5, 50.8) * mm, "end": v(19.25, 55.56) * mm});
            skLineSegment(sketch, "E11.0.4.8", {"start": v(41.24, 55.56) * mm, "end": v(46.74, 55.56) * mm});
            skLineSegment(sketch, "E11.3.4.8", {"start": v(46.74, 55.56) * mm, "end": v(49.5, 50.8) * mm});
            skLineSegment(sketch, "E11.6.4.8", {"start": v(49.5, 50.8) * mm, "end": v(46.74, 46.04) * mm});
            skCircle(sketch, "E11.9.4.8", {"center": v(44, 50.8) * mm, "radius": 4.76 * mm, "construction": true});
            skLineSegment(sketch, "E11.11.4.8", {"start": v(46.74, 46.04) * mm, "end": v(41.24, 46.04) * mm});
            skLineSegment(sketch, "E11.14.4.8", {"start": v(41.24, 46.04) * mm, "end": v(38.5, 50.8) * mm});
            skLineSegment(sketch, "E11.17.4.8", {"start": v(38.5, 50.8) * mm, "end": v(41.24, 55.56) * mm});
            skLineSegment(sketch, "E11.0.5.8", {"start": v(63.24, 55.56) * mm, "end": v(68.74, 55.56) * mm});
            skLineSegment(sketch, "E11.3.5.8", {"start": v(68.74, 55.56) * mm, "end": v(71.49, 50.8) * mm});
            skLineSegment(sketch, "E11.6.5.8", {"start": v(71.49, 50.8) * mm, "end": v(68.74, 46.04) * mm});
            skCircle(sketch, "E11.9.5.8", {"center": v(65.99, 50.8) * mm, "radius": 4.76 * mm, "construction": true});
            skLineSegment(sketch, "E11.11.5.8", {"start": v(68.74, 46.04) * mm, "end": v(63.24, 46.04) * mm});
            skLineSegment(sketch, "E11.14.5.8", {"start": v(63.24, 46.04) * mm, "end": v(60.49, 50.8) * mm});
            skLineSegment(sketch, "E11.17.5.8", {"start": v(60.49, 50.8) * mm, "end": v(63.24, 55.56) * mm});
            skSolve(sketch);
        }
        {
            var Q0;
            Q0 = qSketchRegion(id + "F2", true);
            extrude(context, id + "F3", {"entities" : qUnion([Q0]), "operationType" : NewBodyOperationType.REMOVE, "oppositeDirection" : true, "depth" : 25.4 * mm, "offsetDistance" : 25.4 * mm});
        }
        {
            var Q0;
            Q0=makeQuery(id+"F1.opExtrude","CAP_FACE",FACE,{"disambiguationData":[OSD([sQuery(id+"F0.wireOp",EDGE,"E0")])],"isStart":false});
            var sketch = newSketch(context, id + "F4", { "sketchPlane" : qUnion([Q0])});
            skCircle(sketch, "E12", {"center": v(0, 0) * mm, "radius": 41.28 * mm});
            skCircle(sketch, "E13", {"center": v(0, 0) * mm, "radius": 39.17 * mm});
            skSolve(sketch);
        }
        {
            var Q0;
            Q0 = qSketchRegion(id + "F4", true);
            var Q1;
            Q1=makeQuery(id+"F1.opExtrude","CAP_FACE",FACE,{"disambiguationData":[OSD([sQuery(id+"F0.wireOp",EDGE,"E0")])],"isStart":true});
            extrude(context, id + "F5", {"entities" : qUnion([Q0]), "operationType" : NewBodyOperationType.ADD, "endBound" : BoundingType.UP_TO_SURFACE, "oppositeDirection" : true, "depth" : 25.4 * mm, "endBoundEntityFace" : qUnion([Q1]), "offsetDistance" : 25.4 * mm});
        }
        {
            var Q0;
            Q0=makeQuery(id+"F5.boolean.opBoolean","MERGE",FACE,{"derivedFrom":[makeQuery(id+"F1.opExtrude","CAP_FACE",FACE,{"disambiguationData":[OSD([sQuery(id+"F0.wireOp",EDGE,"E0")])],"isStart":false}),makeQuery(id+"F5.opExtrude","CAP_FACE",FACE,{"disambiguationData":[OSD([sQuery(id+"F4.wireOp",EDGE,"E12"),sQuery(id+"F4.wireOp",EDGE,"E13")])],"isStart":true})]});
            var sketch = newSketch(context, id + "F6", { "sketchPlane" : qUnion([Q0])});
            skLineSegment(sketch, "E14.bottom", {"start": v(-18.21, 35.16) * mm, "end": v(-21.14, 35.16) * mm});
            skLineSegment(sketch, "E14.top", {"start": v(-18.21, 32.55) * mm, "end": v(-21.14, 32.55) * mm});
            skLineSegment(sketch, "E14.left", {"start": v(-18.21, 35.16) * mm, "end": v(-18.21, 32.55) * mm});
            skLineSegment(sketch, "E14.right", {"start": v(-21.14, 35.16) * mm, "end": v(-21.14, 32.55) * mm});
            skLineSegment(sketch, "E15.bottom", {"start": v(-39.62, 1.6) * mm, "end": v(-38.25, 1.6) * mm});
            skLineSegment(sketch, "E15.top", {"start": v(-39.62, -1.97) * mm, "end": v(-38.25, -1.97) * mm});
            skLineSegment(sketch, "E15.left", {"start": v(-39.62, 1.6) * mm, "end": v(-39.62, -1.97) * mm});
            skLineSegment(sketch, "E15.right", {"start": v(-38.25, 1.6) * mm, "end": v(-38.25, -1.97) * mm});
            skLineSegment(sketch, "E16.bottom", {"start": v(18.1, 35.08) * mm, "end": v(20.96, 35.08) * mm});
            skLineSegment(sketch, "E16.top", {"start": v(18.1, 32.55) * mm, "end": v(20.96, 32.55) * mm});
            skLineSegment(sketch, "E16.left", {"start": v(18.1, 35.08) * mm, "end": v(18.1, 32.55) * mm});
            skLineSegment(sketch, "E16.right", {"start": v(20.96, 35.08) * mm, "end": v(20.96, 32.55) * mm});
            skLineSegment(sketch, "E17.bottom", {"start": v(39.8, 2.33) * mm, "end": v(38.06, 2.33) * mm});
            skLineSegment(sketch, "E17.top", {"start": v(39.8, -1.91) * mm, "end": v(38.06, -1.91) * mm});
            skLineSegment(sketch, "E17.left", {"start": v(39.8, 2.33) * mm, "end": v(39.8, -1.91) * mm});
            skLineSegment(sketch, "E17.right", {"start": v(38.06, 2.33) * mm, "end": v(38.06, -1.91) * mm});
            skLineSegment(sketch, "E18.bottom", {"start": v(17.66, -35.42) * mm, "end": v(21.34, -35.42) * mm});
            skLineSegment(sketch, "E18.top", {"start": v(17.66, -32.32) * mm, "end": v(21.34, -32.32) * mm});
            skLineSegment(sketch, "E18.left", {"start": v(17.66, -35.42) * mm, "end": v(17.66, -32.32) * mm});
            skLineSegment(sketch, "E18.right", {"start": v(21.34, -35.42) * mm, "end": v(21.34, -32.32) * mm});
            skLineSegment(sketch, "E19.bottom", {"start": v(-21.76, -32.32) * mm, "end": v(-18.03, -32.32) * mm});
            skLineSegment(sketch, "E19.top", {"start": v(-21.76, -35.17) * mm, "end": v(-18.03, -35.17) * mm});
            skLineSegment(sketch, "E19.left", {"start": v(-21.76, -32.32) * mm, "end": v(-21.76, -35.17) * mm});
            skLineSegment(sketch, "E19.right", {"start": v(-18.03, -32.32) * mm, "end": v(-18.03, -35.17) * mm});
            skSolve(sketch);
        }
        {
            var Q0;
            Q0 = qSketchRegion(id + "F6", true);
            var Q1;
            Q1=makeQuery(id+"F5.boolean.opBoolean","MERGE",FACE,{"derivedFrom":[makeQuery(id+"F1.opExtrude","CAP_FACE",FACE,{"disambiguationData":[OSD([sQuery(id+"F0.wireOp",EDGE,"E0")])],"isStart":true}),makeQuery(id+"F5.opExtrude","CAP_FACE",FACE,{"disambiguationData":[OSD([sQuery(id+"F4.wireOp",EDGE,"E12"),sQuery(id+"F4.wireOp",EDGE,"E13")])],"isStart":false})]});
            extrude(context, id + "F7", {"entities" : qUnion([Q0]), "operationType" : NewBodyOperationType.ADD, "endBound" : BoundingType.UP_TO_SURFACE, "oppositeDirection" : true, "depth" : 25.4 * mm, "endBoundEntityFace" : qUnion([Q1]), "offsetDistance" : 25.4 * mm});
        }
    });
